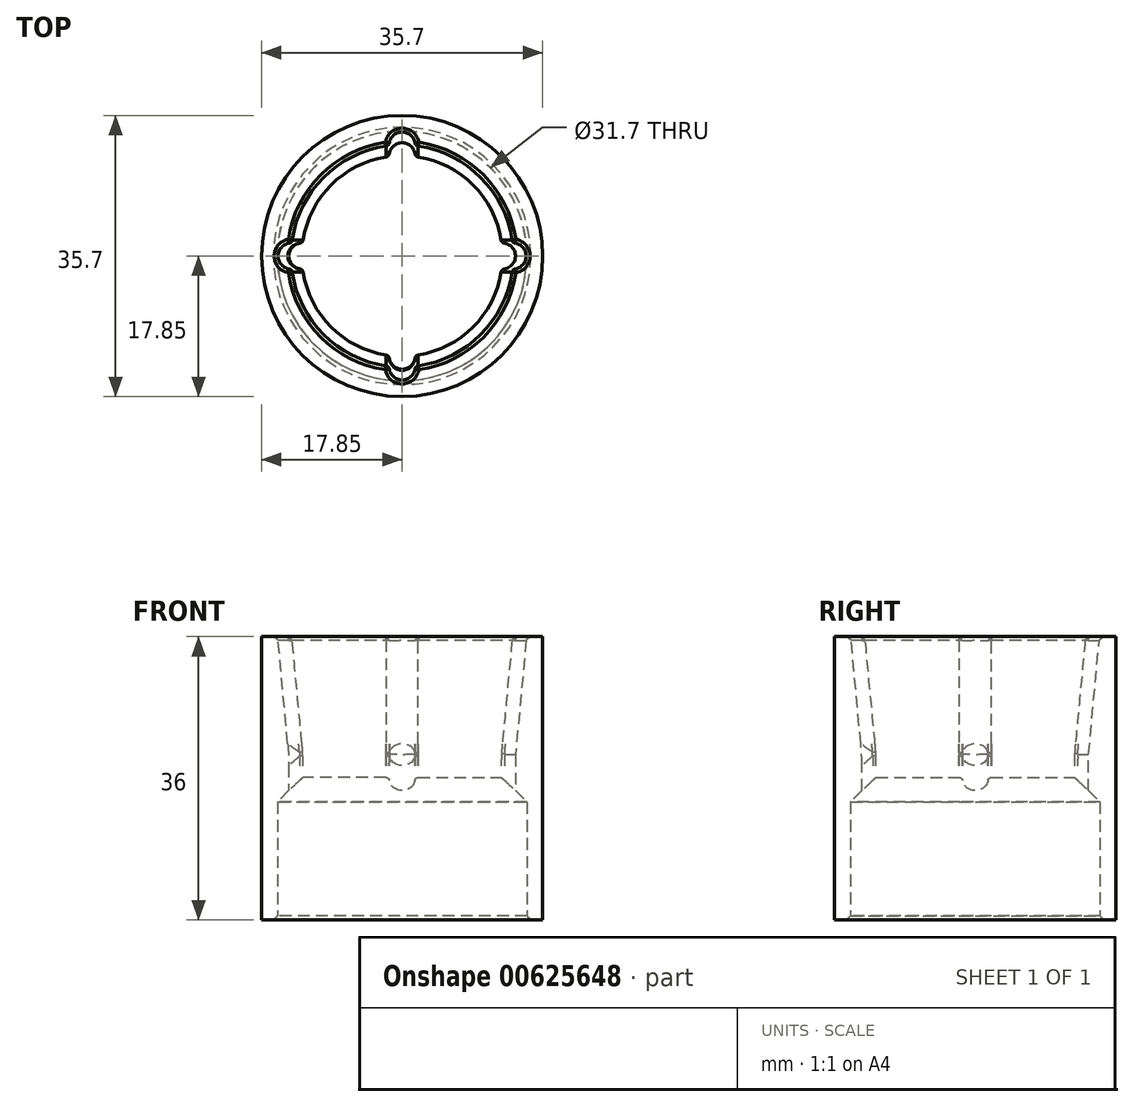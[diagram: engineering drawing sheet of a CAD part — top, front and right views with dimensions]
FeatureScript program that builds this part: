
annotation { "Feature Type Name" : "Feature", "Feature Type Description" : "" }
export const myFeature = defineFeature(function(context is Context, id is Id, definition is map)
    precondition{}
    {
        {
            var Q0;
            Q0=qCreatedBy(makeId("Top.planeOp"),FACE);
            var sketch = newSketch(context, id + "F0", { "sketchPlane" : qUnion([Q0])});
            skCircle(sketch, "E0", {"center": v(0, 0) * mm, "radius": 15.85 * mm});
            skCircle(sketch, "E1", {"center": v(0, 0) * mm, "radius": 17.85 * mm});
            skSolve(sketch);
        }
        {
            var Q0;
            Q0=makeQuery(id+"F0.imprint","IMPRINT",FACE,{"disambiguationData":[TD([[makeQuery(id+"F0.imprint","IMPRINT",EDGE,{"derivedFrom":sQuery(id+"F0.wireOp",EDGE,"E0")}),-1.0]])]});
            extrude(context, id + "F1", {"entities" : qUnion([Q0]), "depth" : 15 * mm, "offsetDistance" : 25 * mm});
        }
        {
            var Q0;
            Q0=makeQuery(id+"F1.opExtrude","CAP_FACE",FACE,{"disambiguationData":[OSD([sQuery(id+"F0.wireOp",EDGE,"E0"),sQuery(id+"F0.wireOp",EDGE,"E1")])],"isStart":false});
            var sketch = newSketch(context, id + "F2", { "sketchPlane" : qUnion([Q0])});
            skCircle(sketch, "E2", {"center": v(0, 0) * mm, "radius": 12.75 * mm});
            skSolve(sketch);
        }
        {
            var Q0;
            Q0=makeQuery(id+"F2.imprint","IMPRINT",FACE,{"disambiguationData":[TD([[makeQuery(id+"F2.imprint","IMPRINT",EDGE,{"derivedFrom":sQuery(id+"F2.wireOp",EDGE,"E2")}),-1.0]])]});
            var Q1;
            Q1=makeQuery(id+"F2.imprint","IMPRINT",FACE,{"disambiguationData":[TD([[makeQuery(id+"F2.imprint","IMPRINT",EDGE,{"derivedFrom":makeQuery(id+"F1.opExtrude","CAP_EDGE",EDGE,{"disambiguationData":[OSD([sQuery(id+"F0.wireOp",EDGE,"E0")])],"isStart":false})}),-1.0]])]});
            extrude(context, id + "F3", {"entities" : qUnion([Q0, Q1]), "operationType" : NewBodyOperationType.ADD, "depth" : 6 * mm, "offsetDistance" : 25 * mm});
        }
        {
            var Q0;
            Q0=makeQuery(id+"F3.opExtrude","CAP_FACE",FACE,{"disambiguationData":[OSD([sQuery(id+"F0.wireOp",EDGE,"E1"),sQuery(id+"F2.wireOp",EDGE,"E2")])],"isStart":false});
            var sketch = newSketch(context, id + "F4", { "sketchPlane" : qUnion([Q0])});
            skCircle(sketch, "E3", {"center": v(0, 12.75) * mm, "radius": 1.65 * mm});
            skCircle(sketch, "E4", {"center": v(12.75, 0) * mm, "radius": 1.65 * mm});
            skCircle(sketch, "E5", {"center": v(0, -12.75) * mm, "radius": 1.65 * mm});
            skCircle(sketch, "E6", {"center": v(-12.75, 0) * mm, "radius": 1.65 * mm});
            skLineSegment(sketch, "E7", {"start": v(-3.96, 14.4) * mm, "end": v(4.3, 14.4) * mm, "construction": true});
            skLineSegment(sketch, "E8", {"start": v(-2.8, -14.4) * mm, "end": v(2.96, -14.4) * mm, "construction": true});
            skLineSegment(sketch, "E9", {"start": v(-12.75, 2.8) * mm, "end": v(-12.75, -2.17) * mm, "construction": true});
            skLineSegment(sketch, "E10", {"start": v(12.75, -1.5) * mm, "end": v(12.75, 1.76) * mm, "construction": true});
            skLineSegment(sketch, "E11", {"start": v(2.2, 12.75) * mm, "end": v(-2.39, 12.75) * mm, "construction": true});
            skLineSegment(sketch, "E12", {"start": v(-3.56, -12.75) * mm, "end": v(1.87, -12.75) * mm, "construction": true});
            skCircle(sketch, "E13.0", {"center": v(0, 0) * mm, "radius": 12.75 * mm});
            skSolve(sketch);
        }
        {
            var Q0;
            Q0=makeQuery(id+"F4.imprint","IMPRINT",FACE,{"disambiguationData":[TD([[makeQuery(id+"F4.imprint","IMPRINT",EDGE,{"derivedFrom":makeQuery(id+"F3.opExtrude","CAP_EDGE",EDGE,{"disambiguationData":[OSD([sQuery(id+"F0.wireOp",EDGE,"E1")])],"isStart":false})}),1.0]])]});
            var Q1;
            {var subQ0=sQuery(id+"F4.wireOp",EDGE,"E5");var subQ1=makeQuery(id+"F3.opExtrude","CAP_EDGE",EDGE,{"disambiguationData":[OSD([sQuery(id+"F2.wireOp",EDGE,"E2")])],"isStart":false});var subQ2=makeQuery(id+"F4.imprint","INTERSECT",VERTEX,{"disambiguationData":[OD(0.0)],"derivedFrom":[subQ1,subQ0]});Q1=makeQuery(id+"F4.imprint","IMPRINT",FACE,{"disambiguationData":[TD([[makeQuery(id+"F4.imprint","IMPRINT",EDGE,{"disambiguationData":[TD([[subQ2,-1.0]])],"derivedFrom":subQ0}),1.0]])]});}
            var Q2;
            {var subQ0=sQuery(id+"F4.wireOp",EDGE,"E13.0");var subQ1=sQuery(id+"F4.wireOp",EDGE,"E6");var subQ2=makeQuery(id+"F4.imprint","INTERSECT",VERTEX,{"disambiguationData":[OD(0.0)],"derivedFrom":[subQ1,subQ0]});Q2=makeQuery(id+"F4.imprint","IMPRINT",FACE,{"disambiguationData":[TD([[makeQuery(id+"F4.imprint","IMPRINT",EDGE,{"disambiguationData":[TD([[subQ2,-1.0]])],"derivedFrom":subQ1}),1.0]])]});}
            var Q3;
            {var subQ0=sQuery(id+"F4.wireOp",EDGE,"E13.0");var subQ1=sQuery(id+"F4.wireOp",EDGE,"E3");var subQ2=makeQuery(id+"F4.imprint","INTERSECT",VERTEX,{"disambiguationData":[OD(0.0)],"derivedFrom":[subQ1,subQ0]});Q3=makeQuery(id+"F4.imprint","IMPRINT",FACE,{"disambiguationData":[TD([[makeQuery(id+"F4.imprint","IMPRINT",EDGE,{"disambiguationData":[TD([[subQ2,-1.0]])],"derivedFrom":subQ1}),1.0]])]});}
            var Q4;
            {var subQ0=sQuery(id+"F4.wireOp",EDGE,"E13.0");var subQ1=sQuery(id+"F4.wireOp",EDGE,"E4");var subQ2=makeQuery(id+"F4.imprint","INTERSECT",VERTEX,{"disambiguationData":[OD(0.0)],"derivedFrom":[subQ1,subQ0]});Q4=makeQuery(id+"F4.imprint","IMPRINT",FACE,{"disambiguationData":[TD([[makeQuery(id+"F4.imprint","IMPRINT",EDGE,{"disambiguationData":[TD([[subQ2,1.0]])],"derivedFrom":subQ1}),1.0]])]});}
            extrude(context, id + "F5", {"entities" : qUnion([Q0, Q1, Q2, Q3, Q4]), "operationType" : NewBodyOperationType.ADD, "depth" : 15 * mm, "offsetDistance" : 25 * mm});
        }
        {
            var Q0;
            Q0=makeQuery(id+"F5.opExtrude","CAP_FACE",FACE,{"disambiguationData":[OSD([sQuery(id+"F0.wireOp",EDGE,"E1"),sQuery(id+"F2.wireOp",EDGE,"E2")])],"isStart":false});
            var sketch = newSketch(context, id + "F6", { "sketchPlane" : qUnion([Q0])});
            skCircle(sketch, "E14", {"center": v(0, 0) * mm, "radius": 14.15 * mm});
            skCircle(sketch, "E15", {"center": v(0, 14.15) * mm, "radius": 1.65 * mm, "construction": true});
            skCircle(sketch, "E16", {"center": v(-14.15, 0) * mm, "radius": 1.65 * mm, "construction": true});
            skCircle(sketch, "E17", {"center": v(14.15, 0) * mm, "radius": 1.65 * mm, "construction": true});
            skCircle(sketch, "E18", {"center": v(0, -14.15) * mm, "radius": 1.65 * mm, "construction": true});
            skLineSegment(sketch, "E19", {"start": v(-14.15, 2.1) * mm, "end": v(-14.15, -2.57) * mm, "construction": true});
            skLineSegment(sketch, "E20", {"start": v(14.15, 2.5) * mm, "end": v(14.15, -1.89) * mm, "construction": true});
            skLineSegment(sketch, "E21", {"start": v(-2.19, -14.15) * mm, "end": v(2.08, -14.15) * mm, "construction": true});
            skLineSegment(sketch, "E22", {"start": v(-2.78, 14.15) * mm, "end": v(3.02, 14.15) * mm, "construction": true});
            skLineSegment(sketch, "E23.bottom", {"start": v(-15.8, -1.65) * mm, "end": v(-12.5, -1.65) * mm});
            skLineSegment(sketch, "E23.top", {"start": v(-15.8, 1.65) * mm, "end": v(-12.5, 1.65) * mm});
            skLineSegment(sketch, "E23.left", {"start": v(-15.8, -1.65) * mm, "end": v(-15.8, 1.65) * mm});
            skLineSegment(sketch, "E23.right", {"start": v(-12.5, -1.65) * mm, "end": v(-12.5, 1.65) * mm, "construction": true});
            skLineSegment(sketch, "E24.bottom", {"start": v(1.65, 12.5) * mm, "end": v(-1.65, 12.5) * mm, "construction": true});
            skLineSegment(sketch, "E24.top", {"start": v(1.65, 15.8) * mm, "end": v(-1.65, 15.8) * mm});
            skLineSegment(sketch, "E24.left", {"start": v(1.65, 12.5) * mm, "end": v(1.65, 15.8) * mm});
            skLineSegment(sketch, "E24.right", {"start": v(-1.65, 12.5) * mm, "end": v(-1.65, 15.8) * mm});
            skLineSegment(sketch, "E25.bottom", {"start": v(15.8, -1.65) * mm, "end": v(12.5, -1.65) * mm});
            skLineSegment(sketch, "E25.top", {"start": v(15.8, 1.65) * mm, "end": v(12.5, 1.65) * mm});
            skLineSegment(sketch, "E25.left", {"start": v(15.8, -1.65) * mm, "end": v(15.8, 1.65) * mm});
            skLineSegment(sketch, "E25.right", {"start": v(12.5, -1.65) * mm, "end": v(12.5, 1.65) * mm, "construction": true});
            skLineSegment(sketch, "E26.bottom", {"start": v(1.65, -15.8) * mm, "end": v(-1.65, -15.8) * mm});
            skLineSegment(sketch, "E26.top", {"start": v(1.65, -12.5) * mm, "end": v(-1.65, -12.5) * mm, "construction": true});
            skLineSegment(sketch, "E26.left", {"start": v(1.65, -15.8) * mm, "end": v(1.65, -12.5) * mm});
            skLineSegment(sketch, "E26.right", {"start": v(-1.65, -15.8) * mm, "end": v(-1.65, -12.5) * mm});
            skSolve(sketch);
        }
        {
            var Q0;
            Q0=makeQuery(id+"F6.imprint","IMPRINT",FACE,{"disambiguationData":[TD([[makeQuery(id+"F6.imprint","IMPRINT",EDGE,{"derivedFrom":makeQuery(id+"F5.opExtrude","CAP_EDGE",EDGE,{"disambiguationData":[OSD([sQuery(id+"F4.wireOp",EDGE,"E13.0")])],"isStart":false})}),-1.0]])]});
            var Q1;
            {var subQ5=sQuery(id+"F6.wireOp",EDGE,"E26.bottom");Q1=makeQuery(id+"F6.imprint","IMPRINT",FACE,{"disambiguationData":[TD([[makeQuery(id+"F6.imprint","IMPRINT",EDGE,{"derivedFrom":subQ5}),-1.0]])]});}
            var Q2;
            {var subQ5=sQuery(id+"F6.wireOp",EDGE,"E25.left");Q2=makeQuery(id+"F6.imprint","IMPRINT",FACE,{"disambiguationData":[TD([[makeQuery(id+"F6.imprint","IMPRINT",EDGE,{"derivedFrom":subQ5}),1.0]])]});}
            var Q3;
            {var subQ5=sQuery(id+"F6.wireOp",EDGE,"E23.left");Q3=makeQuery(id+"F6.imprint","IMPRINT",FACE,{"disambiguationData":[TD([[makeQuery(id+"F6.imprint","IMPRINT",EDGE,{"derivedFrom":subQ5}),-1.0]])]});}
            var Q4;
            {var subQ5=sQuery(id+"F6.wireOp",EDGE,"E24.top");Q4=makeQuery(id+"F6.imprint","IMPRINT",FACE,{"disambiguationData":[TD([[makeQuery(id+"F6.imprint","IMPRINT",EDGE,{"derivedFrom":subQ5}),1.0]])]});}
            extrude(context, id + "F7", {"entities" : qUnion([Q0, Q1, Q2, Q3, Q4]), "operationType" : NewBodyOperationType.REMOVE, "oppositeDirection" : true, "depth" : 15 * mm, "offsetDistance" : 25 * mm});
        }
        {
            var Q0;
            {var subQ0=sQuery(id+"F6.wireOp",EDGE,"E14");Q0=makeQuery(id+"F7.boolean.opBoolean","COPY",EDGE,{"derivedFrom":makeQuery(id+"F7.opExtrude","CAP_EDGE",EDGE,{"disambiguationData":[OSD([subQ0]),TDD([makeQuery(id+"F6.imprint","IMPRINT",EDGE,{"disambiguationData":[TD([[makeQuery(id+"F6.imprint","INTERSECT",VERTEX,{"derivedFrom":[subQ0,sQuery(id+"F6.wireOp",EDGE,"E24.right")]}),-1.0]])],"derivedFrom":subQ0})])],"isStart":false})});}
            var Q1;
            {var subQ0=sQuery(id+"F6.wireOp",EDGE,"E14");Q1=makeQuery(id+"F7.boolean.opBoolean","COPY",EDGE,{"derivedFrom":makeQuery(id+"F7.opExtrude","CAP_EDGE",EDGE,{"disambiguationData":[OSD([subQ0]),TDD([makeQuery(id+"F6.imprint","IMPRINT",EDGE,{"disambiguationData":[TD([[makeQuery(id+"F6.imprint","INTERSECT",VERTEX,{"derivedFrom":[subQ0,sQuery(id+"F6.wireOp",EDGE,"E24.left")]}),1.0]])],"derivedFrom":subQ0})])],"isStart":false})});}
            var Q2;
            {var subQ0=sQuery(id+"F6.wireOp",EDGE,"E14");Q2=makeQuery(id+"F7.boolean.opBoolean","COPY",EDGE,{"derivedFrom":makeQuery(id+"F7.opExtrude","CAP_EDGE",EDGE,{"disambiguationData":[OSD([subQ0]),TDD([makeQuery(id+"F6.imprint","IMPRINT",EDGE,{"disambiguationData":[TD([[makeQuery(id+"F6.imprint","INTERSECT",VERTEX,{"derivedFrom":[subQ0,sQuery(id+"F6.wireOp",EDGE,"E23.bottom")]}),-1.0]])],"derivedFrom":subQ0})])],"isStart":false})});}
            var Q3;
            {var subQ0=sQuery(id+"F6.wireOp",EDGE,"E14");Q3=makeQuery(id+"F7.boolean.opBoolean","COPY",EDGE,{"derivedFrom":makeQuery(id+"F7.opExtrude","CAP_EDGE",EDGE,{"disambiguationData":[OSD([subQ0]),TDD([makeQuery(id+"F6.imprint","IMPRINT",EDGE,{"disambiguationData":[TD([[makeQuery(id+"F6.imprint","INTERSECT",VERTEX,{"derivedFrom":[subQ0,sQuery(id+"F6.wireOp",EDGE,"E26.left")]}),-1.0]])],"derivedFrom":subQ0})])],"isStart":false})});}
            chamfer(context, id + "F8", {"entities" : qUnion([Q0, Q1, Q2, Q3]), "chamferType" : ChamferType.TWO_OFFSETS, "width1" : 1.4 * mm, "oppositeDirection" : false, "width2" : 15 * mm, "tangentPropagation" : true});
        }
        {
            var Q0;
            Q0=makeQuery(id+"F7.boolean.opBoolean","COPY",EDGE,{"derivedFrom":makeQuery(id+"F7.opExtrude","CAP_EDGE",EDGE,{"disambiguationData":[OSD([sQuery(id+"F6.wireOp",EDGE,"E24.top")])],"isStart":false})});
            var Q1;
            Q1=makeQuery(id+"F7.boolean.opBoolean","COPY",EDGE,{"derivedFrom":makeQuery(id+"F7.opExtrude","CAP_EDGE",EDGE,{"disambiguationData":[OSD([sQuery(id+"F6.wireOp",EDGE,"E25.left")])],"isStart":false})});
            chamfer(context, id + "F9", {"entities" : qUnion([Q0, Q1]), "chamferType" : ChamferType.TWO_OFFSETS, "width1" : 1.4 * mm, "oppositeDirection" : false, "width2" : 15 * mm, "tangentPropagation" : true});
        }
        {
            var Q0;
            Q0=makeQuery(id+"F7.boolean.opBoolean","COPY",EDGE,{"derivedFrom":makeQuery(id+"F7.opExtrude","CAP_EDGE",EDGE,{"disambiguationData":[OSD([sQuery(id+"F6.wireOp",EDGE,"E23.left")])],"isStart":false})});
            var Q1;
            Q1=makeQuery(id+"F7.boolean.opBoolean","COPY",EDGE,{"derivedFrom":makeQuery(id+"F7.opExtrude","CAP_EDGE",EDGE,{"disambiguationData":[OSD([sQuery(id+"F6.wireOp",EDGE,"E26.bottom")])],"isStart":false})});
            chamfer(context, id + "F10", {"entities" : qUnion([Q0, Q1]), "chamferType" : ChamferType.TWO_OFFSETS, "width1" : 15 * mm, "oppositeDirection" : false, "width2" : 1.4 * mm, "tangentPropagation" : true});
        }
        {
            var Q0;
            Q0=makeQuery(id+"F8.opChamfer","SPLIT",FACE,{"disambiguationData":[OD(0.0)],"derivedFrom":makeQuery(id+"F7.boolean.opBoolean","COPY",FACE,{"derivedFrom":makeQuery(id+"F7.opExtrude","CAP_FACE",FACE,{"disambiguationData":[OSD([sQuery(id+"F4.wireOp",EDGE,"E13.0"),sQuery(id+"F6.wireOp",EDGE,"E14"),sQuery(id+"F6.wireOp",EDGE,"E23.bottom"),sQuery(id+"F6.wireOp",EDGE,"E23.top"),sQuery(id+"F6.wireOp",EDGE,"E23.left"),sQuery(id+"F6.wireOp",EDGE,"E24.top"),sQuery(id+"F6.wireOp",EDGE,"E24.left"),sQuery(id+"F6.wireOp",EDGE,"E24.right"),sQuery(id+"F6.wireOp",EDGE,"E25.bottom"),sQuery(id+"F6.wireOp",EDGE,"E25.top"),sQuery(id+"F6.wireOp",EDGE,"E25.left"),sQuery(id+"F6.wireOp",EDGE,"E26.bottom"),sQuery(id+"F6.wireOp",EDGE,"E26.left"),sQuery(id+"F6.wireOp",EDGE,"E26.right")])],"isStart":false})})});
            var Q1;
            Q1=makeQuery(id+"F8.opChamfer","SPLIT",FACE,{"disambiguationData":[OD(1.0)],"derivedFrom":makeQuery(id+"F7.boolean.opBoolean","COPY",FACE,{"derivedFrom":makeQuery(id+"F7.opExtrude","CAP_FACE",FACE,{"disambiguationData":[OSD([sQuery(id+"F4.wireOp",EDGE,"E13.0"),sQuery(id+"F6.wireOp",EDGE,"E14"),sQuery(id+"F6.wireOp",EDGE,"E23.bottom"),sQuery(id+"F6.wireOp",EDGE,"E23.top"),sQuery(id+"F6.wireOp",EDGE,"E23.left"),sQuery(id+"F6.wireOp",EDGE,"E24.top"),sQuery(id+"F6.wireOp",EDGE,"E24.left"),sQuery(id+"F6.wireOp",EDGE,"E24.right"),sQuery(id+"F6.wireOp",EDGE,"E25.bottom"),sQuery(id+"F6.wireOp",EDGE,"E25.top"),sQuery(id+"F6.wireOp",EDGE,"E25.left"),sQuery(id+"F6.wireOp",EDGE,"E26.bottom"),sQuery(id+"F6.wireOp",EDGE,"E26.left"),sQuery(id+"F6.wireOp",EDGE,"E26.right")])],"isStart":false})})});
            var Q2;
            Q2=makeQuery(id+"F8.opChamfer","SPLIT",FACE,{"disambiguationData":[OD(2.0)],"derivedFrom":makeQuery(id+"F7.boolean.opBoolean","COPY",FACE,{"derivedFrom":makeQuery(id+"F7.opExtrude","CAP_FACE",FACE,{"disambiguationData":[OSD([sQuery(id+"F4.wireOp",EDGE,"E13.0"),sQuery(id+"F6.wireOp",EDGE,"E14"),sQuery(id+"F6.wireOp",EDGE,"E23.bottom"),sQuery(id+"F6.wireOp",EDGE,"E23.top"),sQuery(id+"F6.wireOp",EDGE,"E23.left"),sQuery(id+"F6.wireOp",EDGE,"E24.top"),sQuery(id+"F6.wireOp",EDGE,"E24.left"),sQuery(id+"F6.wireOp",EDGE,"E24.right"),sQuery(id+"F6.wireOp",EDGE,"E25.bottom"),sQuery(id+"F6.wireOp",EDGE,"E25.top"),sQuery(id+"F6.wireOp",EDGE,"E25.left"),sQuery(id+"F6.wireOp",EDGE,"E26.bottom"),sQuery(id+"F6.wireOp",EDGE,"E26.left"),sQuery(id+"F6.wireOp",EDGE,"E26.right")])],"isStart":false})})});
            var Q3;
            Q3=makeQuery(id+"F8.opChamfer","SPLIT",FACE,{"disambiguationData":[OD(3.0)],"derivedFrom":makeQuery(id+"F7.boolean.opBoolean","COPY",FACE,{"derivedFrom":makeQuery(id+"F7.opExtrude","CAP_FACE",FACE,{"disambiguationData":[OSD([sQuery(id+"F4.wireOp",EDGE,"E13.0"),sQuery(id+"F6.wireOp",EDGE,"E14"),sQuery(id+"F6.wireOp",EDGE,"E23.bottom"),sQuery(id+"F6.wireOp",EDGE,"E23.top"),sQuery(id+"F6.wireOp",EDGE,"E23.left"),sQuery(id+"F6.wireOp",EDGE,"E24.top"),sQuery(id+"F6.wireOp",EDGE,"E24.left"),sQuery(id+"F6.wireOp",EDGE,"E24.right"),sQuery(id+"F6.wireOp",EDGE,"E25.bottom"),sQuery(id+"F6.wireOp",EDGE,"E25.top"),sQuery(id+"F6.wireOp",EDGE,"E25.left"),sQuery(id+"F6.wireOp",EDGE,"E26.bottom"),sQuery(id+"F6.wireOp",EDGE,"E26.left"),sQuery(id+"F6.wireOp",EDGE,"E26.right")])],"isStart":false})})});
            var Q4;
            Q4=makeQuery(id+"F1.opExtrude","SWEPT_BODY",BODY,{"disambiguationData":[OSD([sQuery(id+"F0.wireOp",EDGE,"E0"),sQuery(id+"F0.wireOp",EDGE,"E1")])]});
            extrude(context, id + "F11", {"entities" : qUnion([Q0, Q1, Q2, Q3]), "operationType" : NewBodyOperationType.REMOVE, "endBound" : BoundingType.UP_TO_BODY, "oppositeDirection" : true, "depth" : 2 * mm, "endBoundEntityBody" : qUnion([Q4]), "offsetDistance" : 25 * mm});
        }
        {
            var Q0;
            Q0=makeQuery(id+"F10.opChamfer","BLEND_EDGE",EDGE,{"blendedFrom":[makeQuery(id+"F7.boolean.opBoolean","COPY",EDGE,{"derivedFrom":makeQuery(id+"F7.opExtrude","CAP_EDGE",EDGE,{"disambiguationData":[OSD([sQuery(id+"F6.wireOp",EDGE,"E23.left")])],"isStart":false})}),makeQuery(id+"F7.boolean.opBoolean","COPY",FACE,{"derivedFrom":makeQuery(id+"F7.opExtrude","SWEPT_FACE",FACE,{"disambiguationData":[OSD([sQuery(id+"F6.wireOp",EDGE,"E23.bottom")])]})})],"blendedInto":[makeQuery(id+"F7.boolean.opBoolean","COPY",FACE,{"derivedFrom":makeQuery(id+"F7.opExtrude","SWEPT_FACE",FACE,{"disambiguationData":[OSD([sQuery(id+"F6.wireOp",EDGE,"E23.bottom")])]})})]});
            var Q1;
            {var subQ0=sQuery(id+"F6.wireOp",EDGE,"E26.right");var subQ1=sQuery(id+"F6.wireOp",EDGE,"E26.left");var subQ2=sQuery(id+"F6.wireOp",EDGE,"E26.bottom");var subQ3=sQuery(id+"F6.wireOp",EDGE,"E25.left");var subQ4=sQuery(id+"F6.wireOp",EDGE,"E25.top");var subQ5=sQuery(id+"F6.wireOp",EDGE,"E25.bottom");var subQ6=sQuery(id+"F6.wireOp",EDGE,"E24.right");var subQ7=sQuery(id+"F6.wireOp",EDGE,"E24.left");var subQ8=sQuery(id+"F6.wireOp",EDGE,"E24.top");var subQ9=sQuery(id+"F6.wireOp",EDGE,"E23.left");var subQ10=sQuery(id+"F6.wireOp",EDGE,"E23.top");var subQ11=sQuery(id+"F6.wireOp",EDGE,"E23.bottom");var subQ12=sQuery(id+"F6.wireOp",EDGE,"E14");var subQ13=sQuery(id+"F4.wireOp",EDGE,"E13.0");Q1=makeQuery(id+"F11.boolean.opBoolean","COPY",EDGE,{"derivedFrom":makeQuery(id+"F11.opExtrude","SWEPT_EDGE",EDGE,{"disambiguationData":[OSD([subQ13,subQ12,subQ11,subQ10,subQ9,subQ8,subQ7,subQ6,subQ5,subQ4,subQ3,subQ2,subQ1,subQ0]),TDD([makeQuery(id+"F10.opChamfer","BLEND_VERTEX",VERTEX,{"blendedFrom":[makeQuery(id+"F7.boolean.opBoolean","COPY",EDGE,{"derivedFrom":makeQuery(id+"F7.opExtrude","CAP_EDGE",EDGE,{"disambiguationData":[OSD([subQ9])],"isStart":false})}),makeQuery(id+"F7.boolean.opBoolean","COPY",FACE,{"derivedFrom":makeQuery(id+"F7.opExtrude","SWEPT_FACE",FACE,{"disambiguationData":[OSD([subQ11])]})}),makeQuery(id+"F8.opChamfer","SPLIT",FACE,{"disambiguationData":[OD(0.0)],"derivedFrom":makeQuery(id+"F7.boolean.opBoolean","COPY",FACE,{"derivedFrom":makeQuery(id+"F7.opExtrude","CAP_FACE",FACE,{"disambiguationData":[OSD([subQ13,subQ12,subQ11,subQ10,subQ9,subQ8,subQ7,subQ6,subQ5,subQ4,subQ3,subQ2,subQ1,subQ0])],"isStart":false})})})],"blendedInto":[makeQuery(id+"F7.boolean.opBoolean","COPY",FACE,{"derivedFrom":makeQuery(id+"F7.opExtrude","SWEPT_FACE",FACE,{"disambiguationData":[OSD([subQ11])]})}),makeQuery(id+"F8.opChamfer","SPLIT",FACE,{"disambiguationData":[OD(0.0)],"derivedFrom":makeQuery(id+"F7.boolean.opBoolean","COPY",FACE,{"derivedFrom":makeQuery(id+"F7.opExtrude","CAP_FACE",FACE,{"disambiguationData":[OSD([subQ13,subQ12,subQ11,subQ10,subQ9,subQ8,subQ7,subQ6,subQ5,subQ4,subQ3,subQ2,subQ1,subQ0])],"isStart":false})})})]})])]})});}
            var Q2;
            Q2=makeQuery(id+"F10.opChamfer","BLEND_EDGE",EDGE,{"blendedFrom":[makeQuery(id+"F7.boolean.opBoolean","COPY",EDGE,{"derivedFrom":makeQuery(id+"F7.opExtrude","CAP_EDGE",EDGE,{"disambiguationData":[OSD([sQuery(id+"F6.wireOp",EDGE,"E23.left")])],"isStart":false})}),makeQuery(id+"F7.boolean.opBoolean","COPY",FACE,{"derivedFrom":makeQuery(id+"F7.opExtrude","SWEPT_FACE",FACE,{"disambiguationData":[OSD([sQuery(id+"F6.wireOp",EDGE,"E23.top")])]})})],"blendedInto":[makeQuery(id+"F7.boolean.opBoolean","COPY",FACE,{"derivedFrom":makeQuery(id+"F7.opExtrude","SWEPT_FACE",FACE,{"disambiguationData":[OSD([sQuery(id+"F6.wireOp",EDGE,"E23.top")])]})})]});
            var Q3;
            {var subQ0=sQuery(id+"F6.wireOp",EDGE,"E26.right");var subQ1=sQuery(id+"F6.wireOp",EDGE,"E26.left");var subQ2=sQuery(id+"F6.wireOp",EDGE,"E26.bottom");var subQ3=sQuery(id+"F6.wireOp",EDGE,"E25.left");var subQ4=sQuery(id+"F6.wireOp",EDGE,"E25.top");var subQ5=sQuery(id+"F6.wireOp",EDGE,"E25.bottom");var subQ6=sQuery(id+"F6.wireOp",EDGE,"E24.right");var subQ7=sQuery(id+"F6.wireOp",EDGE,"E24.left");var subQ8=sQuery(id+"F6.wireOp",EDGE,"E24.top");var subQ9=sQuery(id+"F6.wireOp",EDGE,"E23.left");var subQ10=sQuery(id+"F6.wireOp",EDGE,"E23.top");var subQ11=sQuery(id+"F6.wireOp",EDGE,"E23.bottom");var subQ12=sQuery(id+"F6.wireOp",EDGE,"E14");var subQ13=sQuery(id+"F4.wireOp",EDGE,"E13.0");Q3=makeQuery(id+"F11.boolean.opBoolean","COPY",EDGE,{"derivedFrom":makeQuery(id+"F11.opExtrude","SWEPT_EDGE",EDGE,{"disambiguationData":[OSD([subQ13,subQ12,subQ11,subQ10,subQ9,subQ8,subQ7,subQ6,subQ5,subQ4,subQ3,subQ2,subQ1,subQ0]),TDD([makeQuery(id+"F10.opChamfer","BLEND_VERTEX",VERTEX,{"blendedFrom":[makeQuery(id+"F7.boolean.opBoolean","COPY",EDGE,{"derivedFrom":makeQuery(id+"F7.opExtrude","CAP_EDGE",EDGE,{"disambiguationData":[OSD([subQ9])],"isStart":false})}),makeQuery(id+"F7.boolean.opBoolean","COPY",FACE,{"derivedFrom":makeQuery(id+"F7.opExtrude","SWEPT_FACE",FACE,{"disambiguationData":[OSD([subQ10])]})}),makeQuery(id+"F8.opChamfer","SPLIT",FACE,{"disambiguationData":[OD(0.0)],"derivedFrom":makeQuery(id+"F7.boolean.opBoolean","COPY",FACE,{"derivedFrom":makeQuery(id+"F7.opExtrude","CAP_FACE",FACE,{"disambiguationData":[OSD([subQ13,subQ12,subQ11,subQ10,subQ9,subQ8,subQ7,subQ6,subQ5,subQ4,subQ3,subQ2,subQ1,subQ0])],"isStart":false})})})],"blendedInto":[makeQuery(id+"F7.boolean.opBoolean","COPY",FACE,{"derivedFrom":makeQuery(id+"F7.opExtrude","SWEPT_FACE",FACE,{"disambiguationData":[OSD([subQ10])]})}),makeQuery(id+"F8.opChamfer","SPLIT",FACE,{"disambiguationData":[OD(0.0)],"derivedFrom":makeQuery(id+"F7.boolean.opBoolean","COPY",FACE,{"derivedFrom":makeQuery(id+"F7.opExtrude","CAP_FACE",FACE,{"disambiguationData":[OSD([subQ13,subQ12,subQ11,subQ10,subQ9,subQ8,subQ7,subQ6,subQ5,subQ4,subQ3,subQ2,subQ1,subQ0])],"isStart":false})})})]})])]})});}
            var Q4;
            Q4=makeQuery(id+"F9.opChamfer","BLEND_EDGE",EDGE,{"blendedFrom":[makeQuery(id+"F7.boolean.opBoolean","COPY",EDGE,{"derivedFrom":makeQuery(id+"F7.opExtrude","CAP_EDGE",EDGE,{"disambiguationData":[OSD([sQuery(id+"F6.wireOp",EDGE,"E24.top")])],"isStart":false})}),makeQuery(id+"F7.boolean.opBoolean","COPY",FACE,{"derivedFrom":makeQuery(id+"F7.opExtrude","SWEPT_FACE",FACE,{"disambiguationData":[OSD([sQuery(id+"F6.wireOp",EDGE,"E24.right")])]})})],"blendedInto":[makeQuery(id+"F7.boolean.opBoolean","COPY",FACE,{"derivedFrom":makeQuery(id+"F7.opExtrude","SWEPT_FACE",FACE,{"disambiguationData":[OSD([sQuery(id+"F6.wireOp",EDGE,"E24.right")])]})})]});
            var Q5;
            {var subQ0=sQuery(id+"F6.wireOp",EDGE,"E26.right");var subQ1=sQuery(id+"F6.wireOp",EDGE,"E26.left");var subQ2=sQuery(id+"F6.wireOp",EDGE,"E26.bottom");var subQ3=sQuery(id+"F6.wireOp",EDGE,"E25.left");var subQ4=sQuery(id+"F6.wireOp",EDGE,"E25.top");var subQ5=sQuery(id+"F6.wireOp",EDGE,"E25.bottom");var subQ6=sQuery(id+"F6.wireOp",EDGE,"E24.right");var subQ7=sQuery(id+"F6.wireOp",EDGE,"E24.left");var subQ8=sQuery(id+"F6.wireOp",EDGE,"E24.top");var subQ9=sQuery(id+"F6.wireOp",EDGE,"E23.left");var subQ10=sQuery(id+"F6.wireOp",EDGE,"E23.top");var subQ11=sQuery(id+"F6.wireOp",EDGE,"E23.bottom");var subQ12=sQuery(id+"F6.wireOp",EDGE,"E14");var subQ13=sQuery(id+"F4.wireOp",EDGE,"E13.0");Q5=makeQuery(id+"F11.boolean.opBoolean","COPY",EDGE,{"derivedFrom":makeQuery(id+"F11.opExtrude","SWEPT_EDGE",EDGE,{"disambiguationData":[OSD([subQ13,subQ12,subQ11,subQ10,subQ9,subQ8,subQ7,subQ6,subQ5,subQ4,subQ3,subQ2,subQ1,subQ0]),TDD([makeQuery(id+"F9.opChamfer","BLEND_VERTEX",VERTEX,{"blendedFrom":[makeQuery(id+"F7.boolean.opBoolean","COPY",EDGE,{"derivedFrom":makeQuery(id+"F7.opExtrude","CAP_EDGE",EDGE,{"disambiguationData":[OSD([subQ8])],"isStart":false})}),makeQuery(id+"F7.boolean.opBoolean","COPY",FACE,{"derivedFrom":makeQuery(id+"F7.opExtrude","SWEPT_FACE",FACE,{"disambiguationData":[OSD([subQ6])]})}),makeQuery(id+"F8.opChamfer","SPLIT",FACE,{"disambiguationData":[OD(1.0)],"derivedFrom":makeQuery(id+"F7.boolean.opBoolean","COPY",FACE,{"derivedFrom":makeQuery(id+"F7.opExtrude","CAP_FACE",FACE,{"disambiguationData":[OSD([subQ13,subQ12,subQ11,subQ10,subQ9,subQ8,subQ7,subQ6,subQ5,subQ4,subQ3,subQ2,subQ1,subQ0])],"isStart":false})})})],"blendedInto":[makeQuery(id+"F7.boolean.opBoolean","COPY",FACE,{"derivedFrom":makeQuery(id+"F7.opExtrude","SWEPT_FACE",FACE,{"disambiguationData":[OSD([subQ6])]})}),makeQuery(id+"F8.opChamfer","SPLIT",FACE,{"disambiguationData":[OD(1.0)],"derivedFrom":makeQuery(id+"F7.boolean.opBoolean","COPY",FACE,{"derivedFrom":makeQuery(id+"F7.opExtrude","CAP_FACE",FACE,{"disambiguationData":[OSD([subQ13,subQ12,subQ11,subQ10,subQ9,subQ8,subQ7,subQ6,subQ5,subQ4,subQ3,subQ2,subQ1,subQ0])],"isStart":false})})})]})])]})});}
            var Q6;
            {var subQ0=sQuery(id+"F6.wireOp",EDGE,"E26.right");var subQ1=sQuery(id+"F6.wireOp",EDGE,"E26.left");var subQ2=sQuery(id+"F6.wireOp",EDGE,"E26.bottom");var subQ3=sQuery(id+"F6.wireOp",EDGE,"E25.left");var subQ4=sQuery(id+"F6.wireOp",EDGE,"E25.top");var subQ5=sQuery(id+"F6.wireOp",EDGE,"E25.bottom");var subQ6=sQuery(id+"F6.wireOp",EDGE,"E24.right");var subQ7=sQuery(id+"F6.wireOp",EDGE,"E24.left");var subQ8=sQuery(id+"F6.wireOp",EDGE,"E24.top");var subQ9=sQuery(id+"F6.wireOp",EDGE,"E23.left");var subQ10=sQuery(id+"F6.wireOp",EDGE,"E23.top");var subQ11=sQuery(id+"F6.wireOp",EDGE,"E23.bottom");var subQ12=sQuery(id+"F6.wireOp",EDGE,"E14");var subQ13=sQuery(id+"F4.wireOp",EDGE,"E13.0");Q6=makeQuery(id+"F11.boolean.opBoolean","COPY",EDGE,{"derivedFrom":makeQuery(id+"F11.opExtrude","SWEPT_EDGE",EDGE,{"disambiguationData":[OSD([subQ13,subQ12,subQ11,subQ10,subQ9,subQ8,subQ7,subQ6,subQ5,subQ4,subQ3,subQ2,subQ1,subQ0]),TDD([makeQuery(id+"F9.opChamfer","BLEND_VERTEX",VERTEX,{"blendedFrom":[makeQuery(id+"F7.boolean.opBoolean","COPY",EDGE,{"derivedFrom":makeQuery(id+"F7.opExtrude","CAP_EDGE",EDGE,{"disambiguationData":[OSD([subQ8])],"isStart":false})}),makeQuery(id+"F7.boolean.opBoolean","COPY",FACE,{"derivedFrom":makeQuery(id+"F7.opExtrude","SWEPT_FACE",FACE,{"disambiguationData":[OSD([subQ7])]})}),makeQuery(id+"F8.opChamfer","SPLIT",FACE,{"disambiguationData":[OD(1.0)],"derivedFrom":makeQuery(id+"F7.boolean.opBoolean","COPY",FACE,{"derivedFrom":makeQuery(id+"F7.opExtrude","CAP_FACE",FACE,{"disambiguationData":[OSD([subQ13,subQ12,subQ11,subQ10,subQ9,subQ8,subQ7,subQ6,subQ5,subQ4,subQ3,subQ2,subQ1,subQ0])],"isStart":false})})})],"blendedInto":[makeQuery(id+"F7.boolean.opBoolean","COPY",FACE,{"derivedFrom":makeQuery(id+"F7.opExtrude","SWEPT_FACE",FACE,{"disambiguationData":[OSD([subQ7])]})}),makeQuery(id+"F8.opChamfer","SPLIT",FACE,{"disambiguationData":[OD(1.0)],"derivedFrom":makeQuery(id+"F7.boolean.opBoolean","COPY",FACE,{"derivedFrom":makeQuery(id+"F7.opExtrude","CAP_FACE",FACE,{"disambiguationData":[OSD([subQ13,subQ12,subQ11,subQ10,subQ9,subQ8,subQ7,subQ6,subQ5,subQ4,subQ3,subQ2,subQ1,subQ0])],"isStart":false})})})]})])]})});}
            var Q7;
            Q7=makeQuery(id+"F9.opChamfer","BLEND_EDGE",EDGE,{"blendedFrom":[makeQuery(id+"F7.boolean.opBoolean","COPY",EDGE,{"derivedFrom":makeQuery(id+"F7.opExtrude","CAP_EDGE",EDGE,{"disambiguationData":[OSD([sQuery(id+"F6.wireOp",EDGE,"E24.top")])],"isStart":false})}),makeQuery(id+"F7.boolean.opBoolean","COPY",FACE,{"derivedFrom":makeQuery(id+"F7.opExtrude","SWEPT_FACE",FACE,{"disambiguationData":[OSD([sQuery(id+"F6.wireOp",EDGE,"E24.left")])]})})],"blendedInto":[makeQuery(id+"F7.boolean.opBoolean","COPY",FACE,{"derivedFrom":makeQuery(id+"F7.opExtrude","SWEPT_FACE",FACE,{"disambiguationData":[OSD([sQuery(id+"F6.wireOp",EDGE,"E24.left")])]})})]});
            var Q8;
            Q8=makeQuery(id+"F9.opChamfer","BLEND_EDGE",EDGE,{"blendedFrom":[makeQuery(id+"F7.boolean.opBoolean","COPY",EDGE,{"derivedFrom":makeQuery(id+"F7.opExtrude","CAP_EDGE",EDGE,{"disambiguationData":[OSD([sQuery(id+"F6.wireOp",EDGE,"E25.left")])],"isStart":false})}),makeQuery(id+"F7.boolean.opBoolean","COPY",FACE,{"derivedFrom":makeQuery(id+"F7.opExtrude","SWEPT_FACE",FACE,{"disambiguationData":[OSD([sQuery(id+"F6.wireOp",EDGE,"E25.top")])]})})],"blendedInto":[makeQuery(id+"F7.boolean.opBoolean","COPY",FACE,{"derivedFrom":makeQuery(id+"F7.opExtrude","SWEPT_FACE",FACE,{"disambiguationData":[OSD([sQuery(id+"F6.wireOp",EDGE,"E25.top")])]})})]});
            var Q9;
            {var subQ0=sQuery(id+"F6.wireOp",EDGE,"E26.right");var subQ1=sQuery(id+"F6.wireOp",EDGE,"E26.left");var subQ2=sQuery(id+"F6.wireOp",EDGE,"E26.bottom");var subQ3=sQuery(id+"F6.wireOp",EDGE,"E25.left");var subQ4=sQuery(id+"F6.wireOp",EDGE,"E25.top");var subQ5=sQuery(id+"F6.wireOp",EDGE,"E25.bottom");var subQ6=sQuery(id+"F6.wireOp",EDGE,"E24.right");var subQ7=sQuery(id+"F6.wireOp",EDGE,"E24.left");var subQ8=sQuery(id+"F6.wireOp",EDGE,"E24.top");var subQ9=sQuery(id+"F6.wireOp",EDGE,"E23.left");var subQ10=sQuery(id+"F6.wireOp",EDGE,"E23.top");var subQ11=sQuery(id+"F6.wireOp",EDGE,"E23.bottom");var subQ12=sQuery(id+"F6.wireOp",EDGE,"E14");var subQ13=sQuery(id+"F4.wireOp",EDGE,"E13.0");Q9=makeQuery(id+"F11.boolean.opBoolean","COPY",EDGE,{"derivedFrom":makeQuery(id+"F11.opExtrude","SWEPT_EDGE",EDGE,{"disambiguationData":[OSD([subQ13,subQ12,subQ11,subQ10,subQ9,subQ8,subQ7,subQ6,subQ5,subQ4,subQ3,subQ2,subQ1,subQ0]),TDD([makeQuery(id+"F9.opChamfer","BLEND_VERTEX",VERTEX,{"blendedFrom":[makeQuery(id+"F7.boolean.opBoolean","COPY",EDGE,{"derivedFrom":makeQuery(id+"F7.opExtrude","CAP_EDGE",EDGE,{"disambiguationData":[OSD([subQ3])],"isStart":false})}),makeQuery(id+"F7.boolean.opBoolean","COPY",FACE,{"derivedFrom":makeQuery(id+"F7.opExtrude","SWEPT_FACE",FACE,{"disambiguationData":[OSD([subQ4])]})}),makeQuery(id+"F8.opChamfer","SPLIT",FACE,{"disambiguationData":[OD(2.0)],"derivedFrom":makeQuery(id+"F7.boolean.opBoolean","COPY",FACE,{"derivedFrom":makeQuery(id+"F7.opExtrude","CAP_FACE",FACE,{"disambiguationData":[OSD([subQ13,subQ12,subQ11,subQ10,subQ9,subQ8,subQ7,subQ6,subQ5,subQ4,subQ3,subQ2,subQ1,subQ0])],"isStart":false})})})],"blendedInto":[makeQuery(id+"F7.boolean.opBoolean","COPY",FACE,{"derivedFrom":makeQuery(id+"F7.opExtrude","SWEPT_FACE",FACE,{"disambiguationData":[OSD([subQ4])]})}),makeQuery(id+"F8.opChamfer","SPLIT",FACE,{"disambiguationData":[OD(2.0)],"derivedFrom":makeQuery(id+"F7.boolean.opBoolean","COPY",FACE,{"derivedFrom":makeQuery(id+"F7.opExtrude","CAP_FACE",FACE,{"disambiguationData":[OSD([subQ13,subQ12,subQ11,subQ10,subQ9,subQ8,subQ7,subQ6,subQ5,subQ4,subQ3,subQ2,subQ1,subQ0])],"isStart":false})})})]})])]})});}
            var Q10;
            {var subQ0=sQuery(id+"F6.wireOp",EDGE,"E26.right");var subQ1=sQuery(id+"F6.wireOp",EDGE,"E26.left");var subQ2=sQuery(id+"F6.wireOp",EDGE,"E26.bottom");var subQ3=sQuery(id+"F6.wireOp",EDGE,"E25.left");var subQ4=sQuery(id+"F6.wireOp",EDGE,"E25.top");var subQ5=sQuery(id+"F6.wireOp",EDGE,"E25.bottom");var subQ6=sQuery(id+"F6.wireOp",EDGE,"E24.right");var subQ7=sQuery(id+"F6.wireOp",EDGE,"E24.left");var subQ8=sQuery(id+"F6.wireOp",EDGE,"E24.top");var subQ9=sQuery(id+"F6.wireOp",EDGE,"E23.left");var subQ10=sQuery(id+"F6.wireOp",EDGE,"E23.top");var subQ11=sQuery(id+"F6.wireOp",EDGE,"E23.bottom");var subQ12=sQuery(id+"F6.wireOp",EDGE,"E14");var subQ13=sQuery(id+"F4.wireOp",EDGE,"E13.0");Q10=makeQuery(id+"F11.boolean.opBoolean","COPY",EDGE,{"derivedFrom":makeQuery(id+"F11.opExtrude","SWEPT_EDGE",EDGE,{"disambiguationData":[OSD([subQ13,subQ12,subQ11,subQ10,subQ9,subQ8,subQ7,subQ6,subQ5,subQ4,subQ3,subQ2,subQ1,subQ0]),TDD([makeQuery(id+"F9.opChamfer","BLEND_VERTEX",VERTEX,{"blendedFrom":[makeQuery(id+"F7.boolean.opBoolean","COPY",EDGE,{"derivedFrom":makeQuery(id+"F7.opExtrude","CAP_EDGE",EDGE,{"disambiguationData":[OSD([subQ3])],"isStart":false})}),makeQuery(id+"F7.boolean.opBoolean","COPY",FACE,{"derivedFrom":makeQuery(id+"F7.opExtrude","SWEPT_FACE",FACE,{"disambiguationData":[OSD([subQ5])]})}),makeQuery(id+"F8.opChamfer","SPLIT",FACE,{"disambiguationData":[OD(2.0)],"derivedFrom":makeQuery(id+"F7.boolean.opBoolean","COPY",FACE,{"derivedFrom":makeQuery(id+"F7.opExtrude","CAP_FACE",FACE,{"disambiguationData":[OSD([subQ13,subQ12,subQ11,subQ10,subQ9,subQ8,subQ7,subQ6,subQ5,subQ4,subQ3,subQ2,subQ1,subQ0])],"isStart":false})})})],"blendedInto":[makeQuery(id+"F7.boolean.opBoolean","COPY",FACE,{"derivedFrom":makeQuery(id+"F7.opExtrude","SWEPT_FACE",FACE,{"disambiguationData":[OSD([subQ5])]})}),makeQuery(id+"F8.opChamfer","SPLIT",FACE,{"disambiguationData":[OD(2.0)],"derivedFrom":makeQuery(id+"F7.boolean.opBoolean","COPY",FACE,{"derivedFrom":makeQuery(id+"F7.opExtrude","CAP_FACE",FACE,{"disambiguationData":[OSD([subQ13,subQ12,subQ11,subQ10,subQ9,subQ8,subQ7,subQ6,subQ5,subQ4,subQ3,subQ2,subQ1,subQ0])],"isStart":false})})})]})])]})});}
            var Q11;
            Q11=makeQuery(id+"F9.opChamfer","BLEND_EDGE",EDGE,{"blendedFrom":[makeQuery(id+"F7.boolean.opBoolean","COPY",EDGE,{"derivedFrom":makeQuery(id+"F7.opExtrude","CAP_EDGE",EDGE,{"disambiguationData":[OSD([sQuery(id+"F6.wireOp",EDGE,"E25.left")])],"isStart":false})}),makeQuery(id+"F7.boolean.opBoolean","COPY",FACE,{"derivedFrom":makeQuery(id+"F7.opExtrude","SWEPT_FACE",FACE,{"disambiguationData":[OSD([sQuery(id+"F6.wireOp",EDGE,"E25.bottom")])]})})],"blendedInto":[makeQuery(id+"F7.boolean.opBoolean","COPY",FACE,{"derivedFrom":makeQuery(id+"F7.opExtrude","SWEPT_FACE",FACE,{"disambiguationData":[OSD([sQuery(id+"F6.wireOp",EDGE,"E25.bottom")])]})})]});
            var Q12;
            Q12=makeQuery(id+"F10.opChamfer","BLEND_EDGE",EDGE,{"blendedFrom":[makeQuery(id+"F7.boolean.opBoolean","COPY",EDGE,{"derivedFrom":makeQuery(id+"F7.opExtrude","CAP_EDGE",EDGE,{"disambiguationData":[OSD([sQuery(id+"F6.wireOp",EDGE,"E26.bottom")])],"isStart":false})}),makeQuery(id+"F7.boolean.opBoolean","COPY",FACE,{"derivedFrom":makeQuery(id+"F7.opExtrude","SWEPT_FACE",FACE,{"disambiguationData":[OSD([sQuery(id+"F6.wireOp",EDGE,"E26.left")])]})})],"blendedInto":[makeQuery(id+"F7.boolean.opBoolean","COPY",FACE,{"derivedFrom":makeQuery(id+"F7.opExtrude","SWEPT_FACE",FACE,{"disambiguationData":[OSD([sQuery(id+"F6.wireOp",EDGE,"E26.left")])]})})]});
            var Q13;
            Q13=makeQuery(id+"F10.opChamfer","BLEND_EDGE",EDGE,{"blendedFrom":[makeQuery(id+"F7.boolean.opBoolean","COPY",EDGE,{"derivedFrom":makeQuery(id+"F7.opExtrude","CAP_EDGE",EDGE,{"disambiguationData":[OSD([sQuery(id+"F6.wireOp",EDGE,"E26.bottom")])],"isStart":false})}),makeQuery(id+"F7.boolean.opBoolean","COPY",FACE,{"derivedFrom":makeQuery(id+"F7.opExtrude","SWEPT_FACE",FACE,{"disambiguationData":[OSD([sQuery(id+"F6.wireOp",EDGE,"E26.right")])]})})],"blendedInto":[makeQuery(id+"F7.boolean.opBoolean","COPY",FACE,{"derivedFrom":makeQuery(id+"F7.opExtrude","SWEPT_FACE",FACE,{"disambiguationData":[OSD([sQuery(id+"F6.wireOp",EDGE,"E26.right")])]})})]});
            var Q14;
            {var subQ0=sQuery(id+"F6.wireOp",EDGE,"E26.right");var subQ1=sQuery(id+"F6.wireOp",EDGE,"E26.left");var subQ2=sQuery(id+"F6.wireOp",EDGE,"E26.bottom");var subQ3=sQuery(id+"F6.wireOp",EDGE,"E25.left");var subQ4=sQuery(id+"F6.wireOp",EDGE,"E25.top");var subQ5=sQuery(id+"F6.wireOp",EDGE,"E25.bottom");var subQ6=sQuery(id+"F6.wireOp",EDGE,"E24.right");var subQ7=sQuery(id+"F6.wireOp",EDGE,"E24.left");var subQ8=sQuery(id+"F6.wireOp",EDGE,"E24.top");var subQ9=sQuery(id+"F6.wireOp",EDGE,"E23.left");var subQ10=sQuery(id+"F6.wireOp",EDGE,"E23.top");var subQ11=sQuery(id+"F6.wireOp",EDGE,"E23.bottom");var subQ12=sQuery(id+"F6.wireOp",EDGE,"E14");var subQ13=sQuery(id+"F4.wireOp",EDGE,"E13.0");Q14=makeQuery(id+"F11.boolean.opBoolean","COPY",EDGE,{"derivedFrom":makeQuery(id+"F11.opExtrude","SWEPT_EDGE",EDGE,{"disambiguationData":[OSD([subQ13,subQ12,subQ11,subQ10,subQ9,subQ8,subQ7,subQ6,subQ5,subQ4,subQ3,subQ2,subQ1,subQ0]),TDD([makeQuery(id+"F10.opChamfer","BLEND_VERTEX",VERTEX,{"blendedFrom":[makeQuery(id+"F7.boolean.opBoolean","COPY",EDGE,{"derivedFrom":makeQuery(id+"F7.opExtrude","CAP_EDGE",EDGE,{"disambiguationData":[OSD([subQ2])],"isStart":false})}),makeQuery(id+"F7.boolean.opBoolean","COPY",FACE,{"derivedFrom":makeQuery(id+"F7.opExtrude","SWEPT_FACE",FACE,{"disambiguationData":[OSD([subQ0])]})}),makeQuery(id+"F8.opChamfer","SPLIT",FACE,{"disambiguationData":[OD(3.0)],"derivedFrom":makeQuery(id+"F7.boolean.opBoolean","COPY",FACE,{"derivedFrom":makeQuery(id+"F7.opExtrude","CAP_FACE",FACE,{"disambiguationData":[OSD([subQ13,subQ12,subQ11,subQ10,subQ9,subQ8,subQ7,subQ6,subQ5,subQ4,subQ3,subQ2,subQ1,subQ0])],"isStart":false})})})],"blendedInto":[makeQuery(id+"F7.boolean.opBoolean","COPY",FACE,{"derivedFrom":makeQuery(id+"F7.opExtrude","SWEPT_FACE",FACE,{"disambiguationData":[OSD([subQ0])]})}),makeQuery(id+"F8.opChamfer","SPLIT",FACE,{"disambiguationData":[OD(3.0)],"derivedFrom":makeQuery(id+"F7.boolean.opBoolean","COPY",FACE,{"derivedFrom":makeQuery(id+"F7.opExtrude","CAP_FACE",FACE,{"disambiguationData":[OSD([subQ13,subQ12,subQ11,subQ10,subQ9,subQ8,subQ7,subQ6,subQ5,subQ4,subQ3,subQ2,subQ1,subQ0])],"isStart":false})})})]})])]})});}
            var Q15;
            {var subQ0=sQuery(id+"F6.wireOp",EDGE,"E26.right");var subQ1=sQuery(id+"F6.wireOp",EDGE,"E26.left");var subQ2=sQuery(id+"F6.wireOp",EDGE,"E26.bottom");var subQ3=sQuery(id+"F6.wireOp",EDGE,"E25.left");var subQ4=sQuery(id+"F6.wireOp",EDGE,"E25.top");var subQ5=sQuery(id+"F6.wireOp",EDGE,"E25.bottom");var subQ6=sQuery(id+"F6.wireOp",EDGE,"E24.right");var subQ7=sQuery(id+"F6.wireOp",EDGE,"E24.left");var subQ8=sQuery(id+"F6.wireOp",EDGE,"E24.top");var subQ9=sQuery(id+"F6.wireOp",EDGE,"E23.left");var subQ10=sQuery(id+"F6.wireOp",EDGE,"E23.top");var subQ11=sQuery(id+"F6.wireOp",EDGE,"E23.bottom");var subQ12=sQuery(id+"F6.wireOp",EDGE,"E14");var subQ13=sQuery(id+"F4.wireOp",EDGE,"E13.0");Q15=makeQuery(id+"F11.boolean.opBoolean","COPY",EDGE,{"derivedFrom":makeQuery(id+"F11.opExtrude","SWEPT_EDGE",EDGE,{"disambiguationData":[OSD([subQ13,subQ12,subQ11,subQ10,subQ9,subQ8,subQ7,subQ6,subQ5,subQ4,subQ3,subQ2,subQ1,subQ0]),TDD([makeQuery(id+"F10.opChamfer","BLEND_VERTEX",VERTEX,{"blendedFrom":[makeQuery(id+"F7.boolean.opBoolean","COPY",EDGE,{"derivedFrom":makeQuery(id+"F7.opExtrude","CAP_EDGE",EDGE,{"disambiguationData":[OSD([subQ2])],"isStart":false})}),makeQuery(id+"F7.boolean.opBoolean","COPY",FACE,{"derivedFrom":makeQuery(id+"F7.opExtrude","SWEPT_FACE",FACE,{"disambiguationData":[OSD([subQ1])]})}),makeQuery(id+"F8.opChamfer","SPLIT",FACE,{"disambiguationData":[OD(3.0)],"derivedFrom":makeQuery(id+"F7.boolean.opBoolean","COPY",FACE,{"derivedFrom":makeQuery(id+"F7.opExtrude","CAP_FACE",FACE,{"disambiguationData":[OSD([subQ13,subQ12,subQ11,subQ10,subQ9,subQ8,subQ7,subQ6,subQ5,subQ4,subQ3,subQ2,subQ1,subQ0])],"isStart":false})})})],"blendedInto":[makeQuery(id+"F7.boolean.opBoolean","COPY",FACE,{"derivedFrom":makeQuery(id+"F7.opExtrude","SWEPT_FACE",FACE,{"disambiguationData":[OSD([subQ1])]})}),makeQuery(id+"F8.opChamfer","SPLIT",FACE,{"disambiguationData":[OD(3.0)],"derivedFrom":makeQuery(id+"F7.boolean.opBoolean","COPY",FACE,{"derivedFrom":makeQuery(id+"F7.opExtrude","CAP_FACE",FACE,{"disambiguationData":[OSD([subQ13,subQ12,subQ11,subQ10,subQ9,subQ8,subQ7,subQ6,subQ5,subQ4,subQ3,subQ2,subQ1,subQ0])],"isStart":false})})})]})])]})});}
            fillet(context, id + "F12", {"entities" : qUnion([Q0, Q1, Q2, Q3, Q4, Q5, Q6, Q7, Q8, Q9, Q10, Q11, Q12, Q13, Q14, Q15]), "radius" : (3.3 / 2) * mm, "tangentPropagation" : true, "allowEdgeOverflow" : false});
        }
        {
            var Q0;
            {var subQ0=sQuery(id+"F6.wireOp",EDGE,"E14");Q0=makeQuery(id+"F8.opChamfer","BLEND_EDGE",EDGE,{"blendedFrom":[makeQuery(id+"F7.boolean.opBoolean","COPY",EDGE,{"derivedFrom":makeQuery(id+"F7.opExtrude","CAP_EDGE",EDGE,{"disambiguationData":[OSD([subQ0]),TDD([makeQuery(id+"F6.imprint","IMPRINT",EDGE,{"disambiguationData":[TD([[makeQuery(id+"F6.imprint","INTERSECT",VERTEX,{"derivedFrom":[subQ0,sQuery(id+"F6.wireOp",EDGE,"E24.right")]}),-1.0]])],"derivedFrom":subQ0})])],"isStart":false})}),makeQuery(id+"F5.boolean.opBoolean","MERGE",FACE,{"derivedFrom":[makeQuery(id+"F3.opExtrude","SWEPT_FACE",FACE,{"disambiguationData":[OSD([sQuery(id+"F2.wireOp",EDGE,"E2")])]}),makeQuery(id+"F5.opExtrude","SWEPT_FACE",FACE,{"disambiguationData":[OSD([sQuery(id+"F4.wireOp",EDGE,"E13.0")])]})]})],"blendedInto":[makeQuery(id+"F5.boolean.opBoolean","MERGE",FACE,{"derivedFrom":[makeQuery(id+"F3.opExtrude","SWEPT_FACE",FACE,{"disambiguationData":[OSD([sQuery(id+"F2.wireOp",EDGE,"E2")])]}),makeQuery(id+"F5.opExtrude","SWEPT_FACE",FACE,{"disambiguationData":[OSD([sQuery(id+"F4.wireOp",EDGE,"E13.0")])]})]})]});}
            var Q1;
            {var subQ0=sQuery(id+"F6.wireOp",EDGE,"E14");Q1=makeQuery(id+"F8.opChamfer","BLEND_EDGE",EDGE,{"blendedFrom":[makeQuery(id+"F7.boolean.opBoolean","COPY",EDGE,{"derivedFrom":makeQuery(id+"F7.opExtrude","CAP_EDGE",EDGE,{"disambiguationData":[OSD([subQ0]),TDD([makeQuery(id+"F6.imprint","IMPRINT",EDGE,{"disambiguationData":[TD([[makeQuery(id+"F6.imprint","INTERSECT",VERTEX,{"derivedFrom":[subQ0,sQuery(id+"F6.wireOp",EDGE,"E23.bottom")]}),-1.0]])],"derivedFrom":subQ0})])],"isStart":false})}),makeQuery(id+"F5.boolean.opBoolean","MERGE",FACE,{"derivedFrom":[makeQuery(id+"F3.opExtrude","SWEPT_FACE",FACE,{"disambiguationData":[OSD([sQuery(id+"F2.wireOp",EDGE,"E2")])]}),makeQuery(id+"F5.opExtrude","SWEPT_FACE",FACE,{"disambiguationData":[OSD([sQuery(id+"F4.wireOp",EDGE,"E13.0")])]})]})],"blendedInto":[makeQuery(id+"F5.boolean.opBoolean","MERGE",FACE,{"derivedFrom":[makeQuery(id+"F3.opExtrude","SWEPT_FACE",FACE,{"disambiguationData":[OSD([sQuery(id+"F2.wireOp",EDGE,"E2")])]}),makeQuery(id+"F5.opExtrude","SWEPT_FACE",FACE,{"disambiguationData":[OSD([sQuery(id+"F4.wireOp",EDGE,"E13.0")])]})]})]});}
            var Q2;
            {var subQ0=sQuery(id+"F6.wireOp",EDGE,"E14");Q2=makeQuery(id+"F8.opChamfer","BLEND_EDGE",EDGE,{"blendedFrom":[makeQuery(id+"F7.boolean.opBoolean","COPY",EDGE,{"derivedFrom":makeQuery(id+"F7.opExtrude","CAP_EDGE",EDGE,{"disambiguationData":[OSD([subQ0]),TDD([makeQuery(id+"F6.imprint","IMPRINT",EDGE,{"disambiguationData":[TD([[makeQuery(id+"F6.imprint","INTERSECT",VERTEX,{"derivedFrom":[subQ0,sQuery(id+"F6.wireOp",EDGE,"E24.left")]}),1.0]])],"derivedFrom":subQ0})])],"isStart":false})}),makeQuery(id+"F5.boolean.opBoolean","MERGE",FACE,{"derivedFrom":[makeQuery(id+"F3.opExtrude","SWEPT_FACE",FACE,{"disambiguationData":[OSD([sQuery(id+"F2.wireOp",EDGE,"E2")])]}),makeQuery(id+"F5.opExtrude","SWEPT_FACE",FACE,{"disambiguationData":[OSD([sQuery(id+"F4.wireOp",EDGE,"E13.0")])]})]})],"blendedInto":[makeQuery(id+"F5.boolean.opBoolean","MERGE",FACE,{"derivedFrom":[makeQuery(id+"F3.opExtrude","SWEPT_FACE",FACE,{"disambiguationData":[OSD([sQuery(id+"F2.wireOp",EDGE,"E2")])]}),makeQuery(id+"F5.opExtrude","SWEPT_FACE",FACE,{"disambiguationData":[OSD([sQuery(id+"F4.wireOp",EDGE,"E13.0")])]})]})]});}
            var Q3;
            {var subQ0=sQuery(id+"F6.wireOp",EDGE,"E14");Q3=makeQuery(id+"F8.opChamfer","BLEND_EDGE",EDGE,{"blendedFrom":[makeQuery(id+"F7.boolean.opBoolean","COPY",EDGE,{"derivedFrom":makeQuery(id+"F7.opExtrude","CAP_EDGE",EDGE,{"disambiguationData":[OSD([subQ0]),TDD([makeQuery(id+"F6.imprint","IMPRINT",EDGE,{"disambiguationData":[TD([[makeQuery(id+"F6.imprint","INTERSECT",VERTEX,{"derivedFrom":[subQ0,sQuery(id+"F6.wireOp",EDGE,"E26.left")]}),-1.0]])],"derivedFrom":subQ0})])],"isStart":false})}),makeQuery(id+"F5.boolean.opBoolean","MERGE",FACE,{"derivedFrom":[makeQuery(id+"F3.opExtrude","SWEPT_FACE",FACE,{"disambiguationData":[OSD([sQuery(id+"F2.wireOp",EDGE,"E2")])]}),makeQuery(id+"F5.opExtrude","SWEPT_FACE",FACE,{"disambiguationData":[OSD([sQuery(id+"F4.wireOp",EDGE,"E13.0")])]})]})],"blendedInto":[makeQuery(id+"F5.boolean.opBoolean","MERGE",FACE,{"derivedFrom":[makeQuery(id+"F3.opExtrude","SWEPT_FACE",FACE,{"disambiguationData":[OSD([sQuery(id+"F2.wireOp",EDGE,"E2")])]}),makeQuery(id+"F5.opExtrude","SWEPT_FACE",FACE,{"disambiguationData":[OSD([sQuery(id+"F4.wireOp",EDGE,"E13.0")])]})]})]});}
            var Q4;
            {var subQ0=sQuery(id+"F6.wireOp",EDGE,"E26.right");var subQ1=sQuery(id+"F6.wireOp",EDGE,"E26.left");var subQ2=sQuery(id+"F6.wireOp",EDGE,"E26.bottom");var subQ3=sQuery(id+"F6.wireOp",EDGE,"E25.left");var subQ4=sQuery(id+"F6.wireOp",EDGE,"E25.top");var subQ5=sQuery(id+"F6.wireOp",EDGE,"E25.bottom");var subQ6=sQuery(id+"F6.wireOp",EDGE,"E24.right");var subQ7=sQuery(id+"F6.wireOp",EDGE,"E24.left");var subQ8=sQuery(id+"F6.wireOp",EDGE,"E24.top");var subQ9=sQuery(id+"F6.wireOp",EDGE,"E23.left");var subQ10=sQuery(id+"F6.wireOp",EDGE,"E23.top");var subQ11=sQuery(id+"F6.wireOp",EDGE,"E23.bottom");var subQ12=sQuery(id+"F6.wireOp",EDGE,"E14");var subQ13=sQuery(id+"F4.wireOp",EDGE,"E13.0");var subQ14=makeQuery(id+"F7.boolean.opBoolean","COPY",FACE,{"derivedFrom":makeQuery(id+"F7.opExtrude","SWEPT_FACE",FACE,{"disambiguationData":[OSD([subQ11])]})});var subQ15=makeQuery(id+"F7.boolean.opBoolean","COPY",EDGE,{"derivedFrom":makeQuery(id+"F7.opExtrude","CAP_EDGE",EDGE,{"disambiguationData":[OSD([subQ9])],"isStart":false})});Q4=makeQuery(id+"F12.opFillet","BLEND_EDGE",EDGE,{"blendedFrom":[makeQuery(id+"F10.opChamfer","BLEND_EDGE",EDGE,{"blendedFrom":[subQ15,subQ14],"blendedInto":[subQ14]}),makeQuery(id+"F11.boolean.opBoolean","COPY",EDGE,{"derivedFrom":makeQuery(id+"F11.opExtrude","SWEPT_EDGE",EDGE,{"disambiguationData":[OSD([subQ13,subQ12,subQ11,subQ10,subQ9,subQ8,subQ7,subQ6,subQ5,subQ4,subQ3,subQ2,subQ1,subQ0]),TDD([makeQuery(id+"F10.opChamfer","BLEND_VERTEX",VERTEX,{"blendedFrom":[subQ15,subQ14,makeQuery(id+"F8.opChamfer","SPLIT",FACE,{"disambiguationData":[OD(0.0)],"derivedFrom":makeQuery(id+"F7.boolean.opBoolean","COPY",FACE,{"derivedFrom":makeQuery(id+"F7.opExtrude","CAP_FACE",FACE,{"disambiguationData":[OSD([subQ13,subQ12,subQ11,subQ10,subQ9,subQ8,subQ7,subQ6,subQ5,subQ4,subQ3,subQ2,subQ1,subQ0])],"isStart":false})})})],"blendedInto":[subQ14,makeQuery(id+"F8.opChamfer","SPLIT",FACE,{"disambiguationData":[OD(0.0)],"derivedFrom":makeQuery(id+"F7.boolean.opBoolean","COPY",FACE,{"derivedFrom":makeQuery(id+"F7.opExtrude","CAP_FACE",FACE,{"disambiguationData":[OSD([subQ13,subQ12,subQ11,subQ10,subQ9,subQ8,subQ7,subQ6,subQ5,subQ4,subQ3,subQ2,subQ1,subQ0])],"isStart":false})})})]})])]})})],"blendedInto":[]});}
            var Q5;
            {var subQ0=sQuery(id+"F6.wireOp",EDGE,"E26.right");var subQ1=sQuery(id+"F6.wireOp",EDGE,"E26.left");var subQ2=sQuery(id+"F6.wireOp",EDGE,"E26.bottom");var subQ3=sQuery(id+"F6.wireOp",EDGE,"E25.left");var subQ4=sQuery(id+"F6.wireOp",EDGE,"E25.top");var subQ5=sQuery(id+"F6.wireOp",EDGE,"E25.bottom");var subQ6=sQuery(id+"F6.wireOp",EDGE,"E24.right");var subQ7=sQuery(id+"F6.wireOp",EDGE,"E24.left");var subQ8=sQuery(id+"F6.wireOp",EDGE,"E24.top");var subQ9=sQuery(id+"F6.wireOp",EDGE,"E23.left");var subQ10=sQuery(id+"F6.wireOp",EDGE,"E23.top");var subQ11=sQuery(id+"F6.wireOp",EDGE,"E23.bottom");var subQ12=sQuery(id+"F6.wireOp",EDGE,"E14");var subQ13=sQuery(id+"F4.wireOp",EDGE,"E13.0");var subQ14=makeQuery(id+"F7.boolean.opBoolean","COPY",FACE,{"derivedFrom":makeQuery(id+"F7.opExtrude","SWEPT_FACE",FACE,{"disambiguationData":[OSD([subQ1])]})});var subQ15=makeQuery(id+"F7.boolean.opBoolean","COPY",EDGE,{"derivedFrom":makeQuery(id+"F7.opExtrude","CAP_EDGE",EDGE,{"disambiguationData":[OSD([subQ2])],"isStart":false})});Q5=makeQuery(id+"F12.opFillet","BLEND_EDGE",EDGE,{"blendedFrom":[makeQuery(id+"F10.opChamfer","BLEND_EDGE",EDGE,{"blendedFrom":[subQ15,subQ14],"blendedInto":[subQ14]}),makeQuery(id+"F11.boolean.opBoolean","COPY",EDGE,{"derivedFrom":makeQuery(id+"F11.opExtrude","SWEPT_EDGE",EDGE,{"disambiguationData":[OSD([subQ13,subQ12,subQ11,subQ10,subQ9,subQ8,subQ7,subQ6,subQ5,subQ4,subQ3,subQ2,subQ1,subQ0]),TDD([makeQuery(id+"F10.opChamfer","BLEND_VERTEX",VERTEX,{"blendedFrom":[subQ15,subQ14,makeQuery(id+"F8.opChamfer","SPLIT",FACE,{"disambiguationData":[OD(3.0)],"derivedFrom":makeQuery(id+"F7.boolean.opBoolean","COPY",FACE,{"derivedFrom":makeQuery(id+"F7.opExtrude","CAP_FACE",FACE,{"disambiguationData":[OSD([subQ13,subQ12,subQ11,subQ10,subQ9,subQ8,subQ7,subQ6,subQ5,subQ4,subQ3,subQ2,subQ1,subQ0])],"isStart":false})})})],"blendedInto":[subQ14,makeQuery(id+"F8.opChamfer","SPLIT",FACE,{"disambiguationData":[OD(3.0)],"derivedFrom":makeQuery(id+"F7.boolean.opBoolean","COPY",FACE,{"derivedFrom":makeQuery(id+"F7.opExtrude","CAP_FACE",FACE,{"disambiguationData":[OSD([subQ13,subQ12,subQ11,subQ10,subQ9,subQ8,subQ7,subQ6,subQ5,subQ4,subQ3,subQ2,subQ1,subQ0])],"isStart":false})})})]})])]})})],"blendedInto":[]});}
            var Q6;
            {var subQ0=sQuery(id+"F6.wireOp",EDGE,"E26.right");var subQ1=sQuery(id+"F6.wireOp",EDGE,"E26.left");var subQ2=sQuery(id+"F6.wireOp",EDGE,"E26.bottom");var subQ3=sQuery(id+"F6.wireOp",EDGE,"E25.left");var subQ4=sQuery(id+"F6.wireOp",EDGE,"E25.top");var subQ5=sQuery(id+"F6.wireOp",EDGE,"E25.bottom");var subQ6=sQuery(id+"F6.wireOp",EDGE,"E24.right");var subQ7=sQuery(id+"F6.wireOp",EDGE,"E24.left");var subQ8=sQuery(id+"F6.wireOp",EDGE,"E24.top");var subQ9=sQuery(id+"F6.wireOp",EDGE,"E23.left");var subQ10=sQuery(id+"F6.wireOp",EDGE,"E23.top");var subQ11=sQuery(id+"F6.wireOp",EDGE,"E23.bottom");var subQ12=sQuery(id+"F6.wireOp",EDGE,"E14");var subQ13=sQuery(id+"F4.wireOp",EDGE,"E13.0");var subQ14=makeQuery(id+"F7.boolean.opBoolean","COPY",FACE,{"derivedFrom":makeQuery(id+"F7.opExtrude","SWEPT_FACE",FACE,{"disambiguationData":[OSD([subQ6])]})});var subQ15=makeQuery(id+"F7.boolean.opBoolean","COPY",EDGE,{"derivedFrom":makeQuery(id+"F7.opExtrude","CAP_EDGE",EDGE,{"disambiguationData":[OSD([subQ8])],"isStart":false})});Q6=makeQuery(id+"F12.opFillet","BLEND_EDGE",EDGE,{"blendedFrom":[makeQuery(id+"F9.opChamfer","BLEND_EDGE",EDGE,{"blendedFrom":[subQ15,subQ14],"blendedInto":[subQ14]}),makeQuery(id+"F11.boolean.opBoolean","COPY",EDGE,{"derivedFrom":makeQuery(id+"F11.opExtrude","SWEPT_EDGE",EDGE,{"disambiguationData":[OSD([subQ13,subQ12,subQ11,subQ10,subQ9,subQ8,subQ7,subQ6,subQ5,subQ4,subQ3,subQ2,subQ1,subQ0]),TDD([makeQuery(id+"F9.opChamfer","BLEND_VERTEX",VERTEX,{"blendedFrom":[subQ15,subQ14,makeQuery(id+"F8.opChamfer","SPLIT",FACE,{"disambiguationData":[OD(1.0)],"derivedFrom":makeQuery(id+"F7.boolean.opBoolean","COPY",FACE,{"derivedFrom":makeQuery(id+"F7.opExtrude","CAP_FACE",FACE,{"disambiguationData":[OSD([subQ13,subQ12,subQ11,subQ10,subQ9,subQ8,subQ7,subQ6,subQ5,subQ4,subQ3,subQ2,subQ1,subQ0])],"isStart":false})})})],"blendedInto":[subQ14,makeQuery(id+"F8.opChamfer","SPLIT",FACE,{"disambiguationData":[OD(1.0)],"derivedFrom":makeQuery(id+"F7.boolean.opBoolean","COPY",FACE,{"derivedFrom":makeQuery(id+"F7.opExtrude","CAP_FACE",FACE,{"disambiguationData":[OSD([subQ13,subQ12,subQ11,subQ10,subQ9,subQ8,subQ7,subQ6,subQ5,subQ4,subQ3,subQ2,subQ1,subQ0])],"isStart":false})})})]})])]})})],"blendedInto":[]});}
            var Q7;
            {var subQ0=sQuery(id+"F6.wireOp",EDGE,"E26.right");var subQ1=sQuery(id+"F6.wireOp",EDGE,"E26.left");var subQ2=sQuery(id+"F6.wireOp",EDGE,"E26.bottom");var subQ3=sQuery(id+"F6.wireOp",EDGE,"E25.left");var subQ4=sQuery(id+"F6.wireOp",EDGE,"E25.top");var subQ5=sQuery(id+"F6.wireOp",EDGE,"E25.bottom");var subQ6=sQuery(id+"F6.wireOp",EDGE,"E24.right");var subQ7=sQuery(id+"F6.wireOp",EDGE,"E24.left");var subQ8=sQuery(id+"F6.wireOp",EDGE,"E24.top");var subQ9=sQuery(id+"F6.wireOp",EDGE,"E23.left");var subQ10=sQuery(id+"F6.wireOp",EDGE,"E23.top");var subQ11=sQuery(id+"F6.wireOp",EDGE,"E23.bottom");var subQ12=sQuery(id+"F6.wireOp",EDGE,"E14");var subQ13=sQuery(id+"F4.wireOp",EDGE,"E13.0");var subQ14=makeQuery(id+"F7.boolean.opBoolean","COPY",FACE,{"derivedFrom":makeQuery(id+"F7.opExtrude","SWEPT_FACE",FACE,{"disambiguationData":[OSD([subQ4])]})});var subQ15=makeQuery(id+"F7.boolean.opBoolean","COPY",EDGE,{"derivedFrom":makeQuery(id+"F7.opExtrude","CAP_EDGE",EDGE,{"disambiguationData":[OSD([subQ3])],"isStart":false})});Q7=makeQuery(id+"F12.opFillet","BLEND_EDGE",EDGE,{"blendedFrom":[makeQuery(id+"F9.opChamfer","BLEND_EDGE",EDGE,{"blendedFrom":[subQ15,subQ14],"blendedInto":[subQ14]}),makeQuery(id+"F11.boolean.opBoolean","COPY",EDGE,{"derivedFrom":makeQuery(id+"F11.opExtrude","SWEPT_EDGE",EDGE,{"disambiguationData":[OSD([subQ13,subQ12,subQ11,subQ10,subQ9,subQ8,subQ7,subQ6,subQ5,subQ4,subQ3,subQ2,subQ1,subQ0]),TDD([makeQuery(id+"F9.opChamfer","BLEND_VERTEX",VERTEX,{"blendedFrom":[subQ15,subQ14,makeQuery(id+"F8.opChamfer","SPLIT",FACE,{"disambiguationData":[OD(2.0)],"derivedFrom":makeQuery(id+"F7.boolean.opBoolean","COPY",FACE,{"derivedFrom":makeQuery(id+"F7.opExtrude","CAP_FACE",FACE,{"disambiguationData":[OSD([subQ13,subQ12,subQ11,subQ10,subQ9,subQ8,subQ7,subQ6,subQ5,subQ4,subQ3,subQ2,subQ1,subQ0])],"isStart":false})})})],"blendedInto":[subQ14,makeQuery(id+"F8.opChamfer","SPLIT",FACE,{"disambiguationData":[OD(2.0)],"derivedFrom":makeQuery(id+"F7.boolean.opBoolean","COPY",FACE,{"derivedFrom":makeQuery(id+"F7.opExtrude","CAP_FACE",FACE,{"disambiguationData":[OSD([subQ13,subQ12,subQ11,subQ10,subQ9,subQ8,subQ7,subQ6,subQ5,subQ4,subQ3,subQ2,subQ1,subQ0])],"isStart":false})})})]})])]})})],"blendedInto":[]});}
            fillet(context, id + "F13", {"entities" : qUnion([Q0, Q1, Q2, Q3, Q4, Q5, Q6, Q7]), "radius" : 30 * mm, "tangentPropagation" : true, "allowEdgeOverflow" : false});
        }
        {
            var Q0;
            {var subQ0=sQuery(id+"F4.wireOp",EDGE,"E13.0");var subQ1=sQuery(id+"F2.wireOp",EDGE,"E2");var subQ2=sQuery(id+"F6.wireOp",EDGE,"E23.top");var subQ3=sQuery(id+"F6.wireOp",EDGE,"E26.right");var subQ4=sQuery(id+"F6.wireOp",EDGE,"E26.left");var subQ5=sQuery(id+"F6.wireOp",EDGE,"E26.bottom");var subQ6=sQuery(id+"F6.wireOp",EDGE,"E25.left");var subQ7=sQuery(id+"F6.wireOp",EDGE,"E25.top");var subQ8=sQuery(id+"F6.wireOp",EDGE,"E25.bottom");var subQ9=sQuery(id+"F6.wireOp",EDGE,"E24.right");var subQ10=sQuery(id+"F6.wireOp",EDGE,"E24.left");var subQ11=sQuery(id+"F6.wireOp",EDGE,"E24.top");var subQ12=sQuery(id+"F6.wireOp",EDGE,"E23.left");var subQ13=sQuery(id+"F6.wireOp",EDGE,"E23.bottom");var subQ14=sQuery(id+"F6.wireOp",EDGE,"E14");Q0=makeQuery(id+"F11.boolean.opBoolean","COPY",EDGE,{"derivedFrom":makeQuery(id+"F11.opExtrude","SWEPT_EDGE",EDGE,{"disambiguationData":[OSD([subQ1,subQ0,subQ14,subQ13,subQ2,subQ12,subQ11,subQ10,subQ9,subQ8,subQ7,subQ6,subQ5,subQ4,subQ3]),TDD([makeQuery(id+"F8.opChamfer","BLEND_VERTEX",VERTEX,{"blendedFrom":[makeQuery(id+"F7.boolean.opBoolean","COPY",EDGE,{"derivedFrom":makeQuery(id+"F7.opExtrude","CAP_EDGE",EDGE,{"disambiguationData":[OSD([subQ14]),TDD([makeQuery(id+"F6.imprint","IMPRINT",EDGE,{"disambiguationData":[TD([[makeQuery(id+"F6.imprint","INTERSECT",VERTEX,{"derivedFrom":[subQ14,subQ9]}),-1.0]])],"derivedFrom":subQ14})])],"isStart":false})}),makeQuery(id+"F7.boolean.opBoolean","COPY",FACE,{"derivedFrom":makeQuery(id+"F7.opExtrude","CAP_FACE",FACE,{"disambiguationData":[OSD([subQ0,subQ14,subQ13,subQ2,subQ12,subQ11,subQ10,subQ9,subQ8,subQ7,subQ6,subQ5,subQ4,subQ3])],"isStart":false})}),makeQuery(id+"F7.boolean.opBoolean","COPY",FACE,{"derivedFrom":makeQuery(id+"F7.opExtrude","SWEPT_FACE",FACE,{"disambiguationData":[OSD([subQ2])]})}),makeQuery(id+"F5.boolean.opBoolean","MERGE",FACE,{"derivedFrom":[makeQuery(id+"F3.opExtrude","SWEPT_FACE",FACE,{"disambiguationData":[OSD([subQ1])]}),makeQuery(id+"F5.opExtrude","SWEPT_FACE",FACE,{"disambiguationData":[OSD([subQ0])]})]})],"blendedInto":[makeQuery(id+"F7.boolean.opBoolean","COPY",FACE,{"derivedFrom":makeQuery(id+"F7.opExtrude","CAP_FACE",FACE,{"disambiguationData":[OSD([subQ0,subQ14,subQ13,subQ2,subQ12,subQ11,subQ10,subQ9,subQ8,subQ7,subQ6,subQ5,subQ4,subQ3])],"isStart":false})}),makeQuery(id+"F7.boolean.opBoolean","COPY",FACE,{"derivedFrom":makeQuery(id+"F7.opExtrude","SWEPT_FACE",FACE,{"disambiguationData":[OSD([subQ2])]})}),makeQuery(id+"F5.boolean.opBoolean","MERGE",FACE,{"derivedFrom":[makeQuery(id+"F3.opExtrude","SWEPT_FACE",FACE,{"disambiguationData":[OSD([subQ1])]}),makeQuery(id+"F5.opExtrude","SWEPT_FACE",FACE,{"disambiguationData":[OSD([subQ0])]})]})]})])]})});}
            var Q1;
            {var subQ0=sQuery(id+"F6.wireOp",EDGE,"E23.top");var subQ1=sQuery(id+"F6.wireOp",EDGE,"E14");Q1=makeQuery(id+"F8.opChamfer","BLEND_EDGE",EDGE,{"blendedFrom":[makeQuery(id+"F7.boolean.opBoolean","COPY",EDGE,{"derivedFrom":makeQuery(id+"F7.opExtrude","CAP_EDGE",EDGE,{"disambiguationData":[OSD([subQ1]),TDD([makeQuery(id+"F6.imprint","IMPRINT",EDGE,{"disambiguationData":[TD([[makeQuery(id+"F6.imprint","INTERSECT",VERTEX,{"derivedFrom":[subQ1,sQuery(id+"F6.wireOp",EDGE,"E24.right")]}),-1.0]])],"derivedFrom":subQ1})])],"isStart":false})}),makeQuery(id+"F7.boolean.opBoolean","COPY",FACE,{"derivedFrom":makeQuery(id+"F7.opExtrude","SWEPT_FACE",FACE,{"disambiguationData":[OSD([subQ0])]})})],"blendedInto":[makeQuery(id+"F7.boolean.opBoolean","COPY",FACE,{"derivedFrom":makeQuery(id+"F7.opExtrude","SWEPT_FACE",FACE,{"disambiguationData":[OSD([subQ0])]})})]});}
            var Q2;
            {var subQ0=sQuery(id+"F4.wireOp",EDGE,"E13.0");var subQ1=sQuery(id+"F2.wireOp",EDGE,"E2");var subQ2=sQuery(id+"F6.wireOp",EDGE,"E23.bottom");var subQ3=sQuery(id+"F6.wireOp",EDGE,"E26.right");var subQ4=sQuery(id+"F6.wireOp",EDGE,"E26.left");var subQ5=sQuery(id+"F6.wireOp",EDGE,"E26.bottom");var subQ6=sQuery(id+"F6.wireOp",EDGE,"E25.left");var subQ7=sQuery(id+"F6.wireOp",EDGE,"E25.top");var subQ8=sQuery(id+"F6.wireOp",EDGE,"E25.bottom");var subQ9=sQuery(id+"F6.wireOp",EDGE,"E24.right");var subQ10=sQuery(id+"F6.wireOp",EDGE,"E24.left");var subQ11=sQuery(id+"F6.wireOp",EDGE,"E24.top");var subQ12=sQuery(id+"F6.wireOp",EDGE,"E23.left");var subQ13=sQuery(id+"F6.wireOp",EDGE,"E23.top");var subQ14=sQuery(id+"F6.wireOp",EDGE,"E14");Q2=makeQuery(id+"F11.boolean.opBoolean","COPY",EDGE,{"derivedFrom":makeQuery(id+"F11.opExtrude","SWEPT_EDGE",EDGE,{"disambiguationData":[OSD([subQ1,subQ0,subQ14,subQ2,subQ13,subQ12,subQ11,subQ10,subQ9,subQ8,subQ7,subQ6,subQ5,subQ4,subQ3]),TDD([makeQuery(id+"F8.opChamfer","BLEND_VERTEX",VERTEX,{"blendedFrom":[makeQuery(id+"F7.boolean.opBoolean","COPY",EDGE,{"derivedFrom":makeQuery(id+"F7.opExtrude","CAP_EDGE",EDGE,{"disambiguationData":[OSD([subQ14]),TDD([makeQuery(id+"F6.imprint","IMPRINT",EDGE,{"disambiguationData":[TD([[makeQuery(id+"F6.imprint","INTERSECT",VERTEX,{"derivedFrom":[subQ14,subQ2]}),-1.0]])],"derivedFrom":subQ14})])],"isStart":false})}),makeQuery(id+"F7.boolean.opBoolean","COPY",FACE,{"derivedFrom":makeQuery(id+"F7.opExtrude","CAP_FACE",FACE,{"disambiguationData":[OSD([subQ0,subQ14,subQ2,subQ13,subQ12,subQ11,subQ10,subQ9,subQ8,subQ7,subQ6,subQ5,subQ4,subQ3])],"isStart":false})}),makeQuery(id+"F7.boolean.opBoolean","COPY",FACE,{"derivedFrom":makeQuery(id+"F7.opExtrude","SWEPT_FACE",FACE,{"disambiguationData":[OSD([subQ2])]})}),makeQuery(id+"F5.boolean.opBoolean","MERGE",FACE,{"derivedFrom":[makeQuery(id+"F3.opExtrude","SWEPT_FACE",FACE,{"disambiguationData":[OSD([subQ1])]}),makeQuery(id+"F5.opExtrude","SWEPT_FACE",FACE,{"disambiguationData":[OSD([subQ0])]})]})],"blendedInto":[makeQuery(id+"F7.boolean.opBoolean","COPY",FACE,{"derivedFrom":makeQuery(id+"F7.opExtrude","CAP_FACE",FACE,{"disambiguationData":[OSD([subQ0,subQ14,subQ2,subQ13,subQ12,subQ11,subQ10,subQ9,subQ8,subQ7,subQ6,subQ5,subQ4,subQ3])],"isStart":false})}),makeQuery(id+"F7.boolean.opBoolean","COPY",FACE,{"derivedFrom":makeQuery(id+"F7.opExtrude","SWEPT_FACE",FACE,{"disambiguationData":[OSD([subQ2])]})}),makeQuery(id+"F5.boolean.opBoolean","MERGE",FACE,{"derivedFrom":[makeQuery(id+"F3.opExtrude","SWEPT_FACE",FACE,{"disambiguationData":[OSD([subQ1])]}),makeQuery(id+"F5.opExtrude","SWEPT_FACE",FACE,{"disambiguationData":[OSD([subQ0])]})]})]})])]})});}
            var Q3;
            {var subQ0=sQuery(id+"F6.wireOp",EDGE,"E23.bottom");var subQ1=sQuery(id+"F6.wireOp",EDGE,"E14");Q3=makeQuery(id+"F8.opChamfer","BLEND_EDGE",EDGE,{"blendedFrom":[makeQuery(id+"F7.boolean.opBoolean","COPY",EDGE,{"derivedFrom":makeQuery(id+"F7.opExtrude","CAP_EDGE",EDGE,{"disambiguationData":[OSD([subQ1]),TDD([makeQuery(id+"F6.imprint","IMPRINT",EDGE,{"disambiguationData":[TD([[makeQuery(id+"F6.imprint","INTERSECT",VERTEX,{"derivedFrom":[subQ1,subQ0]}),-1.0]])],"derivedFrom":subQ1})])],"isStart":false})}),makeQuery(id+"F7.boolean.opBoolean","COPY",FACE,{"derivedFrom":makeQuery(id+"F7.opExtrude","SWEPT_FACE",FACE,{"disambiguationData":[OSD([subQ0])]})})],"blendedInto":[makeQuery(id+"F7.boolean.opBoolean","COPY",FACE,{"derivedFrom":makeQuery(id+"F7.opExtrude","SWEPT_FACE",FACE,{"disambiguationData":[OSD([subQ0])]})})]});}
            var Q4;
            {var subQ0=sQuery(id+"F6.wireOp",EDGE,"E24.right");var subQ1=sQuery(id+"F6.wireOp",EDGE,"E14");Q4=makeQuery(id+"F8.opChamfer","BLEND_EDGE",EDGE,{"blendedFrom":[makeQuery(id+"F7.boolean.opBoolean","COPY",EDGE,{"derivedFrom":makeQuery(id+"F7.opExtrude","CAP_EDGE",EDGE,{"disambiguationData":[OSD([subQ1]),TDD([makeQuery(id+"F6.imprint","IMPRINT",EDGE,{"disambiguationData":[TD([[makeQuery(id+"F6.imprint","INTERSECT",VERTEX,{"derivedFrom":[subQ1,subQ0]}),-1.0]])],"derivedFrom":subQ1})])],"isStart":false})}),makeQuery(id+"F7.boolean.opBoolean","COPY",FACE,{"derivedFrom":makeQuery(id+"F7.opExtrude","SWEPT_FACE",FACE,{"disambiguationData":[OSD([subQ0])]})})],"blendedInto":[makeQuery(id+"F7.boolean.opBoolean","COPY",FACE,{"derivedFrom":makeQuery(id+"F7.opExtrude","SWEPT_FACE",FACE,{"disambiguationData":[OSD([subQ0])]})})]});}
            var Q5;
            {var subQ0=sQuery(id+"F6.wireOp",EDGE,"E24.left");var subQ1=sQuery(id+"F6.wireOp",EDGE,"E14");Q5=makeQuery(id+"F8.opChamfer","BLEND_EDGE",EDGE,{"blendedFrom":[makeQuery(id+"F7.boolean.opBoolean","COPY",EDGE,{"derivedFrom":makeQuery(id+"F7.opExtrude","CAP_EDGE",EDGE,{"disambiguationData":[OSD([subQ1]),TDD([makeQuery(id+"F6.imprint","IMPRINT",EDGE,{"disambiguationData":[TD([[makeQuery(id+"F6.imprint","INTERSECT",VERTEX,{"derivedFrom":[subQ1,subQ0]}),1.0]])],"derivedFrom":subQ1})])],"isStart":false})}),makeQuery(id+"F7.boolean.opBoolean","COPY",FACE,{"derivedFrom":makeQuery(id+"F7.opExtrude","SWEPT_FACE",FACE,{"disambiguationData":[OSD([subQ0])]})})],"blendedInto":[makeQuery(id+"F7.boolean.opBoolean","COPY",FACE,{"derivedFrom":makeQuery(id+"F7.opExtrude","SWEPT_FACE",FACE,{"disambiguationData":[OSD([subQ0])]})})]});}
            var Q6;
            {var subQ0=sQuery(id+"F6.wireOp",EDGE,"E25.top");var subQ1=sQuery(id+"F6.wireOp",EDGE,"E14");Q6=makeQuery(id+"F8.opChamfer","BLEND_EDGE",EDGE,{"blendedFrom":[makeQuery(id+"F7.boolean.opBoolean","COPY",EDGE,{"derivedFrom":makeQuery(id+"F7.opExtrude","CAP_EDGE",EDGE,{"disambiguationData":[OSD([subQ1]),TDD([makeQuery(id+"F6.imprint","IMPRINT",EDGE,{"disambiguationData":[TD([[makeQuery(id+"F6.imprint","INTERSECT",VERTEX,{"derivedFrom":[subQ1,sQuery(id+"F6.wireOp",EDGE,"E24.left")]}),1.0]])],"derivedFrom":subQ1})])],"isStart":false})}),makeQuery(id+"F7.boolean.opBoolean","COPY",FACE,{"derivedFrom":makeQuery(id+"F7.opExtrude","SWEPT_FACE",FACE,{"disambiguationData":[OSD([subQ0])]})})],"blendedInto":[makeQuery(id+"F7.boolean.opBoolean","COPY",FACE,{"derivedFrom":makeQuery(id+"F7.opExtrude","SWEPT_FACE",FACE,{"disambiguationData":[OSD([subQ0])]})})]});}
            var Q7;
            {var subQ0=sQuery(id+"F6.wireOp",EDGE,"E25.bottom");var subQ1=sQuery(id+"F6.wireOp",EDGE,"E14");Q7=makeQuery(id+"F8.opChamfer","BLEND_EDGE",EDGE,{"blendedFrom":[makeQuery(id+"F7.boolean.opBoolean","COPY",EDGE,{"derivedFrom":makeQuery(id+"F7.opExtrude","CAP_EDGE",EDGE,{"disambiguationData":[OSD([subQ1]),TDD([makeQuery(id+"F6.imprint","IMPRINT",EDGE,{"disambiguationData":[TD([[makeQuery(id+"F6.imprint","INTERSECT",VERTEX,{"derivedFrom":[subQ1,sQuery(id+"F6.wireOp",EDGE,"E26.left")]}),-1.0]])],"derivedFrom":subQ1})])],"isStart":false})}),makeQuery(id+"F7.boolean.opBoolean","COPY",FACE,{"derivedFrom":makeQuery(id+"F7.opExtrude","SWEPT_FACE",FACE,{"disambiguationData":[OSD([subQ0])]})})],"blendedInto":[makeQuery(id+"F7.boolean.opBoolean","COPY",FACE,{"derivedFrom":makeQuery(id+"F7.opExtrude","SWEPT_FACE",FACE,{"disambiguationData":[OSD([subQ0])]})})]});}
            var Q8;
            {var subQ0=sQuery(id+"F6.wireOp",EDGE,"E26.left");var subQ1=sQuery(id+"F6.wireOp",EDGE,"E14");Q8=makeQuery(id+"F8.opChamfer","BLEND_EDGE",EDGE,{"blendedFrom":[makeQuery(id+"F7.boolean.opBoolean","COPY",EDGE,{"derivedFrom":makeQuery(id+"F7.opExtrude","CAP_EDGE",EDGE,{"disambiguationData":[OSD([subQ1]),TDD([makeQuery(id+"F6.imprint","IMPRINT",EDGE,{"disambiguationData":[TD([[makeQuery(id+"F6.imprint","INTERSECT",VERTEX,{"derivedFrom":[subQ1,subQ0]}),-1.0]])],"derivedFrom":subQ1})])],"isStart":false})}),makeQuery(id+"F7.boolean.opBoolean","COPY",FACE,{"derivedFrom":makeQuery(id+"F7.opExtrude","SWEPT_FACE",FACE,{"disambiguationData":[OSD([subQ0])]})})],"blendedInto":[makeQuery(id+"F7.boolean.opBoolean","COPY",FACE,{"derivedFrom":makeQuery(id+"F7.opExtrude","SWEPT_FACE",FACE,{"disambiguationData":[OSD([subQ0])]})})]});}
            var Q9;
            {var subQ0=sQuery(id+"F6.wireOp",EDGE,"E26.right");var subQ1=sQuery(id+"F6.wireOp",EDGE,"E14");Q9=makeQuery(id+"F8.opChamfer","BLEND_EDGE",EDGE,{"blendedFrom":[makeQuery(id+"F7.boolean.opBoolean","COPY",EDGE,{"derivedFrom":makeQuery(id+"F7.opExtrude","CAP_EDGE",EDGE,{"disambiguationData":[OSD([subQ1]),TDD([makeQuery(id+"F6.imprint","IMPRINT",EDGE,{"disambiguationData":[TD([[makeQuery(id+"F6.imprint","INTERSECT",VERTEX,{"derivedFrom":[subQ1,sQuery(id+"F6.wireOp",EDGE,"E23.bottom")]}),-1.0]])],"derivedFrom":subQ1})])],"isStart":false})}),makeQuery(id+"F7.boolean.opBoolean","COPY",FACE,{"derivedFrom":makeQuery(id+"F7.opExtrude","SWEPT_FACE",FACE,{"disambiguationData":[OSD([subQ0])]})})],"blendedInto":[makeQuery(id+"F7.boolean.opBoolean","COPY",FACE,{"derivedFrom":makeQuery(id+"F7.opExtrude","SWEPT_FACE",FACE,{"disambiguationData":[OSD([subQ0])]})})]});}
            fillet(context, id + "F14", {"entities" : qUnion([Q0, Q1, Q2, Q3, Q4, Q5, Q6, Q7, Q8, Q9]), "radius" : 0.5 * mm, "tangentPropagation" : true, "allowEdgeOverflow" : false});
        }
        {
            var Q0;
            {var subQ0=sQuery(id+"F6.wireOp",EDGE,"E14");Q0=makeQuery(id+"F8.opChamfer","BLEND_EDGE",EDGE,{"blendedFrom":[makeQuery(id+"F7.boolean.opBoolean","COPY",EDGE,{"derivedFrom":makeQuery(id+"F7.opExtrude","CAP_EDGE",EDGE,{"disambiguationData":[OSD([subQ0]),TDD([makeQuery(id+"F6.imprint","IMPRINT",EDGE,{"disambiguationData":[TD([[makeQuery(id+"F6.imprint","INTERSECT",VERTEX,{"derivedFrom":[subQ0,sQuery(id+"F6.wireOp",EDGE,"E23.bottom")]}),-1.0]])],"derivedFrom":subQ0})])],"isStart":false})}),makeQuery(id+"F5.opExtrude","CAP_FACE",FACE,{"disambiguationData":[OSD([sQuery(id+"F0.wireOp",EDGE,"E1"),sQuery(id+"F4.wireOp",EDGE,"E13.0")])],"isStart":false})],"blendedInto":[makeQuery(id+"F5.opExtrude","CAP_FACE",FACE,{"disambiguationData":[OSD([sQuery(id+"F0.wireOp",EDGE,"E1"),sQuery(id+"F4.wireOp",EDGE,"E13.0")])],"isStart":false})]});}
            var Q1;
            Q1=makeQuery(id+"F12.opFillet","BLEND_EDGE",EDGE,{"blendedFrom":[makeQuery(id+"F10.opChamfer","BLEND_EDGE",EDGE,{"blendedFrom":[makeQuery(id+"F7.boolean.opBoolean","COPY",EDGE,{"derivedFrom":makeQuery(id+"F7.opExtrude","CAP_EDGE",EDGE,{"disambiguationData":[OSD([sQuery(id+"F6.wireOp",EDGE,"E23.left")])],"isStart":false})}),makeQuery(id+"F7.boolean.opBoolean","COPY",FACE,{"derivedFrom":makeQuery(id+"F7.opExtrude","SWEPT_FACE",FACE,{"disambiguationData":[OSD([sQuery(id+"F6.wireOp",EDGE,"E23.bottom")])]})})],"blendedInto":[makeQuery(id+"F7.boolean.opBoolean","COPY",FACE,{"derivedFrom":makeQuery(id+"F7.opExtrude","SWEPT_FACE",FACE,{"disambiguationData":[OSD([sQuery(id+"F6.wireOp",EDGE,"E23.bottom")])]})})]}),makeQuery(id+"F5.opExtrude","CAP_FACE",FACE,{"disambiguationData":[OSD([sQuery(id+"F0.wireOp",EDGE,"E1"),sQuery(id+"F4.wireOp",EDGE,"E13.0")])],"isStart":false})],"blendedInto":[makeQuery(id+"F5.opExtrude","CAP_FACE",FACE,{"disambiguationData":[OSD([sQuery(id+"F0.wireOp",EDGE,"E1"),sQuery(id+"F4.wireOp",EDGE,"E13.0")])],"isStart":false})]});
            var Q2;
            {var subQ0=sQuery(id+"F6.wireOp",EDGE,"E14");Q2=makeQuery(id+"F8.opChamfer","BLEND_EDGE",EDGE,{"blendedFrom":[makeQuery(id+"F7.boolean.opBoolean","COPY",EDGE,{"derivedFrom":makeQuery(id+"F7.opExtrude","CAP_EDGE",EDGE,{"disambiguationData":[OSD([subQ0]),TDD([makeQuery(id+"F6.imprint","IMPRINT",EDGE,{"disambiguationData":[TD([[makeQuery(id+"F6.imprint","INTERSECT",VERTEX,{"derivedFrom":[subQ0,sQuery(id+"F6.wireOp",EDGE,"E24.right")]}),-1.0]])],"derivedFrom":subQ0})])],"isStart":false})}),makeQuery(id+"F5.opExtrude","CAP_FACE",FACE,{"disambiguationData":[OSD([sQuery(id+"F0.wireOp",EDGE,"E1"),sQuery(id+"F4.wireOp",EDGE,"E13.0")])],"isStart":false})],"blendedInto":[makeQuery(id+"F5.opExtrude","CAP_FACE",FACE,{"disambiguationData":[OSD([sQuery(id+"F0.wireOp",EDGE,"E1"),sQuery(id+"F4.wireOp",EDGE,"E13.0")])],"isStart":false})]});}
            var Q3;
            Q3=makeQuery(id+"F12.opFillet","BLEND_EDGE",EDGE,{"blendedFrom":[makeQuery(id+"F9.opChamfer","BLEND_EDGE",EDGE,{"blendedFrom":[makeQuery(id+"F7.boolean.opBoolean","COPY",EDGE,{"derivedFrom":makeQuery(id+"F7.opExtrude","CAP_EDGE",EDGE,{"disambiguationData":[OSD([sQuery(id+"F6.wireOp",EDGE,"E24.top")])],"isStart":false})}),makeQuery(id+"F7.boolean.opBoolean","COPY",FACE,{"derivedFrom":makeQuery(id+"F7.opExtrude","SWEPT_FACE",FACE,{"disambiguationData":[OSD([sQuery(id+"F6.wireOp",EDGE,"E24.left")])]})})],"blendedInto":[makeQuery(id+"F7.boolean.opBoolean","COPY",FACE,{"derivedFrom":makeQuery(id+"F7.opExtrude","SWEPT_FACE",FACE,{"disambiguationData":[OSD([sQuery(id+"F6.wireOp",EDGE,"E24.left")])]})})]}),makeQuery(id+"F5.opExtrude","CAP_FACE",FACE,{"disambiguationData":[OSD([sQuery(id+"F0.wireOp",EDGE,"E1"),sQuery(id+"F4.wireOp",EDGE,"E13.0")])],"isStart":false})],"blendedInto":[makeQuery(id+"F5.opExtrude","CAP_FACE",FACE,{"disambiguationData":[OSD([sQuery(id+"F0.wireOp",EDGE,"E1"),sQuery(id+"F4.wireOp",EDGE,"E13.0")])],"isStart":false})]});
            var Q4;
            {var subQ0=sQuery(id+"F6.wireOp",EDGE,"E14");Q4=makeQuery(id+"F8.opChamfer","BLEND_EDGE",EDGE,{"blendedFrom":[makeQuery(id+"F7.boolean.opBoolean","COPY",EDGE,{"derivedFrom":makeQuery(id+"F7.opExtrude","CAP_EDGE",EDGE,{"disambiguationData":[OSD([subQ0]),TDD([makeQuery(id+"F6.imprint","IMPRINT",EDGE,{"disambiguationData":[TD([[makeQuery(id+"F6.imprint","INTERSECT",VERTEX,{"derivedFrom":[subQ0,sQuery(id+"F6.wireOp",EDGE,"E24.left")]}),1.0]])],"derivedFrom":subQ0})])],"isStart":false})}),makeQuery(id+"F5.opExtrude","CAP_FACE",FACE,{"disambiguationData":[OSD([sQuery(id+"F0.wireOp",EDGE,"E1"),sQuery(id+"F4.wireOp",EDGE,"E13.0")])],"isStart":false})],"blendedInto":[makeQuery(id+"F5.opExtrude","CAP_FACE",FACE,{"disambiguationData":[OSD([sQuery(id+"F0.wireOp",EDGE,"E1"),sQuery(id+"F4.wireOp",EDGE,"E13.0")])],"isStart":false})]});}
            var Q5;
            Q5=makeQuery(id+"F12.opFillet","BLEND_EDGE",EDGE,{"blendedFrom":[makeQuery(id+"F9.opChamfer","BLEND_EDGE",EDGE,{"blendedFrom":[makeQuery(id+"F7.boolean.opBoolean","COPY",EDGE,{"derivedFrom":makeQuery(id+"F7.opExtrude","CAP_EDGE",EDGE,{"disambiguationData":[OSD([sQuery(id+"F6.wireOp",EDGE,"E25.left")])],"isStart":false})}),makeQuery(id+"F7.boolean.opBoolean","COPY",FACE,{"derivedFrom":makeQuery(id+"F7.opExtrude","SWEPT_FACE",FACE,{"disambiguationData":[OSD([sQuery(id+"F6.wireOp",EDGE,"E25.bottom")])]})})],"blendedInto":[makeQuery(id+"F7.boolean.opBoolean","COPY",FACE,{"derivedFrom":makeQuery(id+"F7.opExtrude","SWEPT_FACE",FACE,{"disambiguationData":[OSD([sQuery(id+"F6.wireOp",EDGE,"E25.bottom")])]})})]}),makeQuery(id+"F5.opExtrude","CAP_FACE",FACE,{"disambiguationData":[OSD([sQuery(id+"F0.wireOp",EDGE,"E1"),sQuery(id+"F4.wireOp",EDGE,"E13.0")])],"isStart":false})],"blendedInto":[makeQuery(id+"F5.opExtrude","CAP_FACE",FACE,{"disambiguationData":[OSD([sQuery(id+"F0.wireOp",EDGE,"E1"),sQuery(id+"F4.wireOp",EDGE,"E13.0")])],"isStart":false})]});
            var Q6;
            {var subQ0=sQuery(id+"F6.wireOp",EDGE,"E14");Q6=makeQuery(id+"F8.opChamfer","BLEND_EDGE",EDGE,{"blendedFrom":[makeQuery(id+"F7.boolean.opBoolean","COPY",EDGE,{"derivedFrom":makeQuery(id+"F7.opExtrude","CAP_EDGE",EDGE,{"disambiguationData":[OSD([subQ0]),TDD([makeQuery(id+"F6.imprint","IMPRINT",EDGE,{"disambiguationData":[TD([[makeQuery(id+"F6.imprint","INTERSECT",VERTEX,{"derivedFrom":[subQ0,sQuery(id+"F6.wireOp",EDGE,"E26.left")]}),-1.0]])],"derivedFrom":subQ0})])],"isStart":false})}),makeQuery(id+"F5.opExtrude","CAP_FACE",FACE,{"disambiguationData":[OSD([sQuery(id+"F0.wireOp",EDGE,"E1"),sQuery(id+"F4.wireOp",EDGE,"E13.0")])],"isStart":false})],"blendedInto":[makeQuery(id+"F5.opExtrude","CAP_FACE",FACE,{"disambiguationData":[OSD([sQuery(id+"F0.wireOp",EDGE,"E1"),sQuery(id+"F4.wireOp",EDGE,"E13.0")])],"isStart":false})]});}
            var Q7;
            Q7=makeQuery(id+"F12.opFillet","BLEND_EDGE",EDGE,{"blendedFrom":[makeQuery(id+"F10.opChamfer","BLEND_EDGE",EDGE,{"blendedFrom":[makeQuery(id+"F7.boolean.opBoolean","COPY",EDGE,{"derivedFrom":makeQuery(id+"F7.opExtrude","CAP_EDGE",EDGE,{"disambiguationData":[OSD([sQuery(id+"F6.wireOp",EDGE,"E26.bottom")])],"isStart":false})}),makeQuery(id+"F7.boolean.opBoolean","COPY",FACE,{"derivedFrom":makeQuery(id+"F7.opExtrude","SWEPT_FACE",FACE,{"disambiguationData":[OSD([sQuery(id+"F6.wireOp",EDGE,"E26.left")])]})})],"blendedInto":[makeQuery(id+"F7.boolean.opBoolean","COPY",FACE,{"derivedFrom":makeQuery(id+"F7.opExtrude","SWEPT_FACE",FACE,{"disambiguationData":[OSD([sQuery(id+"F6.wireOp",EDGE,"E26.left")])]})})]}),makeQuery(id+"F5.opExtrude","CAP_FACE",FACE,{"disambiguationData":[OSD([sQuery(id+"F0.wireOp",EDGE,"E1"),sQuery(id+"F4.wireOp",EDGE,"E13.0")])],"isStart":false})],"blendedInto":[makeQuery(id+"F5.opExtrude","CAP_FACE",FACE,{"disambiguationData":[OSD([sQuery(id+"F0.wireOp",EDGE,"E1"),sQuery(id+"F4.wireOp",EDGE,"E13.0")])],"isStart":false})]});
            chamfer(context, id + "F15", {"entities" : qUnion([Q0, Q1, Q2, Q3, Q4, Q5, Q6, Q7]), "width" : 0.5 * mm});
        }
        {
            var Q0;
            Q0=qCreatedBy(makeId("Right.planeOp"),FACE);
            var sketch = newSketch(context, id + "F16", { "sketchPlane" : qUnion([Q0])});
            skLineSegment(sketch, "E27.0", {"start": v(-15.85, 15) * mm, "end": v(15.85, 15) * mm});
            skLineSegment(sketch, "E28", {"start": v(0, 15) * mm, "end": v(0, 20) * mm});
            skLineSegment(sketch, "E29", {"start": v(0, 20) * mm, "end": v(-10.85, 20) * mm});
            skLineSegment(sketch, "E30", {"start": v(-10.85, 20) * mm, "end": v(-15.85, 15) * mm});
            skSolve(sketch);
        }
        {
            var Q0;
            {var subQ2=sQuery(id+"F16.wireOp",EDGE,"E28");Q0=makeQuery(id+"F16.imprint","IMPRINT",FACE,{"disambiguationData":[TD([[makeQuery(id+"F16.imprint","IMPRINT",EDGE,{"derivedFrom":subQ2}),1.0]])]});}
            var Q1;
            Q1=sQuery(id+"F16.wireOp",EDGE,"E28");
            revolve(context, id + "F17", {"operationType" : NewBodyOperationType.REMOVE, "entities" : qUnion([Q0]), "axis" : qUnion([Q1]), "revolveType" : RevolveType.FULL, "oppositeDirection" : true});
        }
        {
            var Q0;
            Q0=makeQuery(id+"F1.opExtrude","CAP_EDGE",EDGE,{"disambiguationData":[OSD([sQuery(id+"F0.wireOp",EDGE,"E0")])],"isStart":true});
            chamfer(context, id + "F18", {"entities" : qUnion([Q0]), "width" : 0.5 * mm, "tangentPropagation" : true});
        }
    });
